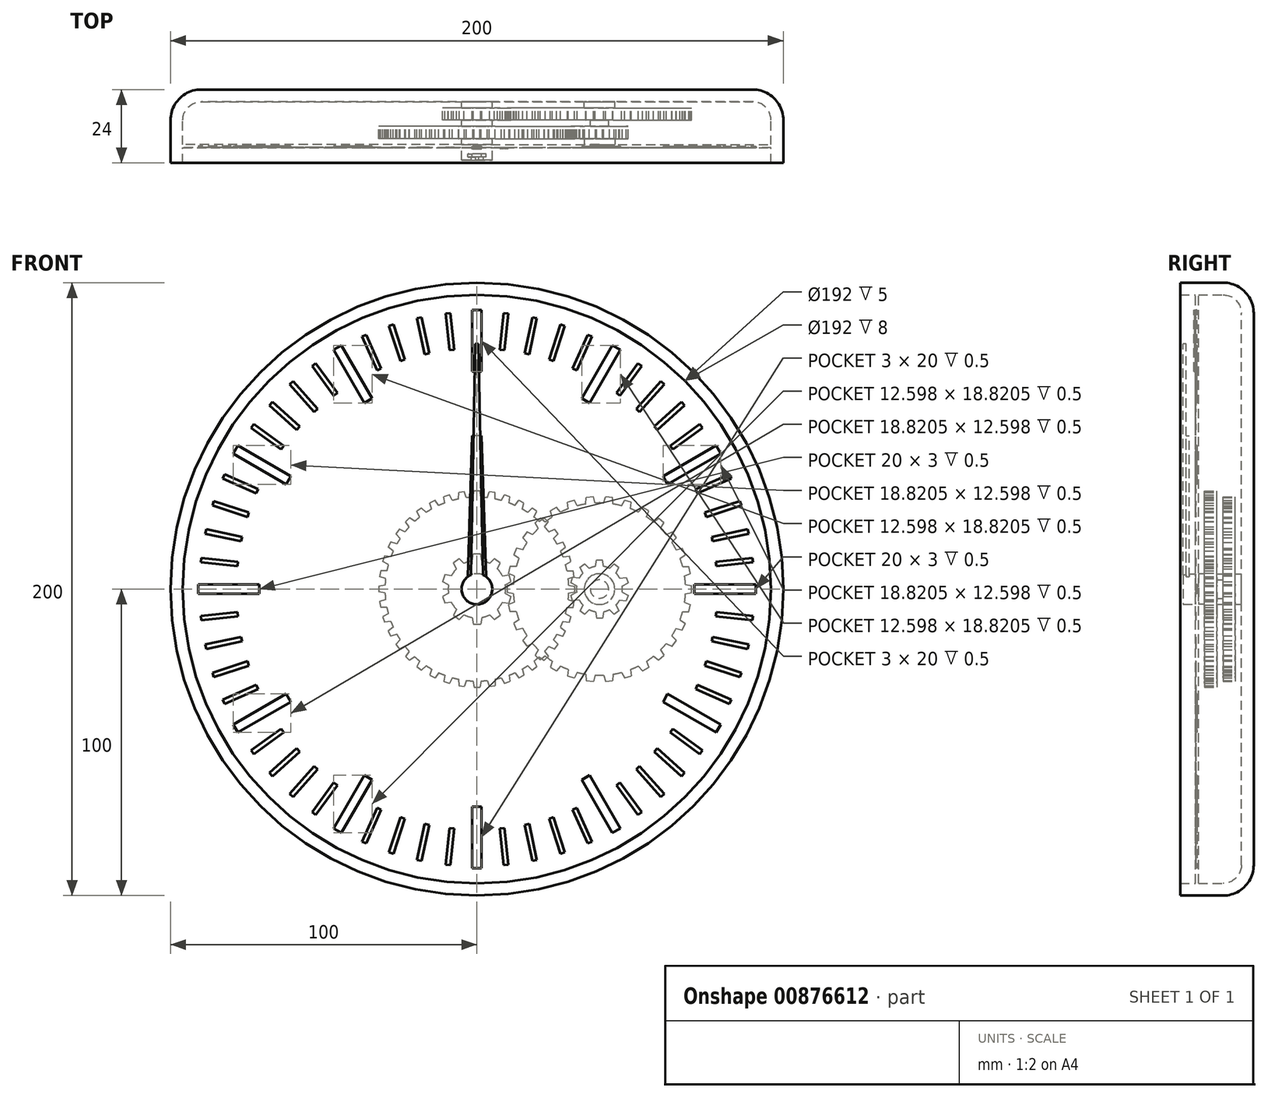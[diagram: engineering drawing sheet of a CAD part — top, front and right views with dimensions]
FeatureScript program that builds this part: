
annotation { "Feature Type Name" : "Feature", "Feature Type Description" : "" }
export const myFeature = defineFeature(function(context is Context, id is Id, definition is map)
    precondition{}
    {
        {
            var Q0;
            Q0=qCreatedBy(makeId("Front.planeOp"),FACE);
            var sketch = newSketch(context, id + "F0", { "sketchPlane" : qUnion([Q0])});
            skCircle(sketch, "E0", {"center": v(0, 0) * mm, "radius": 100 * mm});
            skSolve(sketch);
        }
        {
            var Q0;
            Q0 = qSketchRegion(id + "F0", true);
            extrude(context, id + "F1", {"entities" : qUnion([Q0]), "depth" : 24 * mm, "offsetDistance" : 25 * mm});
        }
        {
            var Q0;
            Q0=makeQuery(id+"F1.opExtrude","CAP_EDGE",EDGE,{"disambiguationData":[OSD([sQuery(id+"F0.wireOp",EDGE,"E0")])],"isStart":true});
            fillet(context, id + "F2", {"entities" : qUnion([Q0]), "radius" : 10 * mm, "tangentPropagation" : true, "allowEdgeOverflow" : false});
        }
        {
            var Q0;
            Q0=makeQuery(id+"F1.opExtrude","CAP_FACE",FACE,{"disambiguationData":[OSD([sQuery(id+"F0.wireOp",EDGE,"E0")])],"isStart":false});
            shell(context, id + "F3", {"entities" : qUnion([Q0]), "thickness" : 4 * mm});
        }
        {
            var Q0;
            {var subQ0=sQuery(id+"F0.wireOp",EDGE,"E0");Q0=makeQuery(id+"F3.opShell","OFFSET_FACE",FACE,{"disambiguationData":[OSD([subQ0]),TDD([makeQuery(id+"F1.opExtrude","CAP_FACE",FACE,{"disambiguationData":[OSD([subQ0])],"isStart":true})])]});}
            var sketch = newSketch(context, id + "F4", { "sketchPlane" : qUnion([Q0])});
            skCircle(sketch, "E1", {"center": v(0, 0) * mm, "radius": 3 * mm});
            skCircle(sketch, "E2", {"center": v(0, 0) * mm, "radius": 5 * mm});
            skCircle(sketch, "E3", {"center": v(40, 0) * mm, "radius": 3 * mm});
            skCircle(sketch, "E4", {"center": v(40, 0) * mm, "radius": 5 * mm});
            skSolve(sketch);
        }
        {
            var Q0;
            Q0 = qSketchRegion(id + "F4", true);
            extrude(context, id + "F5", {"entities" : qUnion([Q0]), "operationType" : NewBodyOperationType.ADD, "depth" : 2 * mm, "offsetDistance" : 25 * mm});
        }
        {
            var Q0;
            {var subQ0=sQuery(id+"F0.wireOp",EDGE,"E0");Q0=makeQuery(id+"F5.boolean.opBoolean","SPLIT",FACE,{"disambiguationData":[TD([makeQuery(id+"F5.opExtrude","SWEPT_FACE",FACE,{"disambiguationData":[OSD([sQuery(id+"F4.wireOp",EDGE,"E1")])]})])],"derivedFrom":makeQuery(id+"F3.opShell","OFFSET_FACE",FACE,{"disambiguationData":[OSD([subQ0]),TDD([makeQuery(id+"F1.opExtrude","CAP_FACE",FACE,{"disambiguationData":[OSD([subQ0])],"isStart":true})])]})});}
            extrude(context, id + "F6", {"entities" : qUnion([Q0]), "depth" : 19 * mm, "offsetDistance" : 25 * mm});
        }
        {
            var Q0;
            {var subQ0=sQuery(id+"F0.wireOp",EDGE,"E0");Q0=makeQuery(id+"F5.boolean.opBoolean","SPLIT",FACE,{"disambiguationData":[TD([makeQuery(id+"F5.opExtrude","SWEPT_FACE",FACE,{"disambiguationData":[OSD([sQuery(id+"F4.wireOp",EDGE,"E3")])]})])],"derivedFrom":makeQuery(id+"F3.opShell","OFFSET_FACE",FACE,{"disambiguationData":[OSD([subQ0]),TDD([makeQuery(id+"F1.opExtrude","CAP_FACE",FACE,{"disambiguationData":[OSD([subQ0])],"isStart":true})])]})});}
            extrude(context, id + "F7", {"entities" : qUnion([Q0]), "depth" : 8 * mm, "offsetDistance" : 25 * mm});
        }
        {
            var Q0;
            Q0=makeQuery(id+"F5.opExtrude","CAP_FACE",FACE,{"disambiguationData":[OSD([sQuery(id+"F4.wireOp",EDGE,"E1"),sQuery(id+"F4.wireOp",EDGE,"E2")])],"isStart":false});
            var sketch = newSketch(context, id + "F8", { "sketchPlane" : qUnion([Q0])});
            skCircle(sketch, "E5", {"center": v(0, 0) * mm, "radius": 9.38 * mm});
            skLineSegment(sketch, "E6", {"start": v(1.55, 9.25) * mm, "end": v(1.18, 11.38) * mm});
            skLineSegment(sketch, "E7", {"start": v(1.18, 11.38) * mm, "end": v(0, 11.38) * mm});
            skLineSegment(sketch, "E8.MirrorCS", {"start": v(-1.18, 11.38) * mm, "end": v(0, 11.38) * mm});
            skLineSegment(sketch, "E9.MirrorCS", {"start": v(-1.55, 9.25) * mm, "end": v(-1.18, 11.38) * mm});
            skLineSegment(sketch, "E10.1.0", {"start": v(-4.18, 8.4) * mm, "end": v(-5.73, 9.9) * mm});
            skLineSegment(sketch, "E10.1.1", {"start": v(-5.73, 9.9) * mm, "end": v(-6.69, 9.2) * mm});
            skLineSegment(sketch, "E10.1.2", {"start": v(-7.64, 8.51) * mm, "end": v(-6.69, 9.2) * mm});
            skLineSegment(sketch, "E10.1.3", {"start": v(-6.7, 6.57) * mm, "end": v(-7.64, 8.51) * mm});
            skLineSegment(sketch, "E10.2.0", {"start": v(-8.31, 4.33) * mm, "end": v(-10.45, 4.64) * mm});
            skLineSegment(sketch, "E10.2.1", {"start": v(-10.45, 4.64) * mm, "end": v(-10.82, 3.52) * mm});
            skLineSegment(sketch, "E10.2.2", {"start": v(-11.18, 2.4) * mm, "end": v(-10.82, 3.52) * mm});
            skLineSegment(sketch, "E10.2.3", {"start": v(-9.27, 1.38) * mm, "end": v(-11.18, 2.4) * mm});
            skLineSegment(sketch, "E11.1.3.0", {"start": v(-9.27, -1.38) * mm, "end": v(-11.18, -2.4) * mm});
            skLineSegment(sketch, "E11.3.3.0", {"start": v(-11.18, -2.4) * mm, "end": v(-10.82, -3.52) * mm});
            skLineSegment(sketch, "E11.6.3.0", {"start": v(-10.45, -4.64) * mm, "end": v(-10.82, -3.52) * mm});
            skLineSegment(sketch, "E11.9.3.0", {"start": v(-8.31, -4.33) * mm, "end": v(-10.45, -4.64) * mm});
            skLineSegment(sketch, "E11.1.4.0", {"start": v(-6.7, -6.57) * mm, "end": v(-7.64, -8.51) * mm});
            skLineSegment(sketch, "E11.3.4.0", {"start": v(-7.64, -8.51) * mm, "end": v(-6.69, -9.2) * mm});
            skLineSegment(sketch, "E11.6.4.0", {"start": v(-5.73, -9.9) * mm, "end": v(-6.69, -9.2) * mm});
            skLineSegment(sketch, "E11.9.4.0", {"start": v(-4.18, -8.4) * mm, "end": v(-5.73, -9.9) * mm});
            skLineSegment(sketch, "E11.1.5.0", {"start": v(-1.55, -9.25) * mm, "end": v(-1.18, -11.38) * mm});
            skLineSegment(sketch, "E11.3.5.0", {"start": v(-1.18, -11.38) * mm, "end": v(0, -11.38) * mm});
            skLineSegment(sketch, "E11.6.5.0", {"start": v(1.18, -11.38) * mm, "end": v(0, -11.38) * mm});
            skLineSegment(sketch, "E11.9.5.0", {"start": v(1.55, -9.25) * mm, "end": v(1.18, -11.38) * mm});
            skLineSegment(sketch, "E11.1.6.0", {"start": v(4.18, -8.4) * mm, "end": v(5.73, -9.9) * mm});
            skLineSegment(sketch, "E11.3.6.0", {"start": v(5.73, -9.9) * mm, "end": v(6.69, -9.2) * mm});
            skLineSegment(sketch, "E11.6.6.0", {"start": v(7.64, -8.51) * mm, "end": v(6.69, -9.2) * mm});
            skLineSegment(sketch, "E11.9.6.0", {"start": v(6.7, -6.57) * mm, "end": v(7.64, -8.51) * mm});
            skLineSegment(sketch, "E11.1.7.0", {"start": v(8.31, -4.33) * mm, "end": v(10.45, -4.64) * mm});
            skLineSegment(sketch, "E11.3.7.0", {"start": v(10.45, -4.64) * mm, "end": v(10.82, -3.52) * mm});
            skLineSegment(sketch, "E11.6.7.0", {"start": v(11.18, -2.4) * mm, "end": v(10.82, -3.52) * mm});
            skLineSegment(sketch, "E11.9.7.0", {"start": v(9.27, -1.38) * mm, "end": v(11.18, -2.4) * mm});
            skLineSegment(sketch, "E11.1.8.0", {"start": v(9.27, 1.38) * mm, "end": v(11.18, 2.4) * mm});
            skLineSegment(sketch, "E11.3.8.0", {"start": v(11.18, 2.4) * mm, "end": v(10.82, 3.52) * mm});
            skLineSegment(sketch, "E11.6.8.0", {"start": v(10.45, 4.64) * mm, "end": v(10.82, 3.52) * mm});
            skLineSegment(sketch, "E11.9.8.0", {"start": v(8.31, 4.33) * mm, "end": v(10.45, 4.64) * mm});
            skLineSegment(sketch, "E11.1.9.0", {"start": v(6.7, 6.57) * mm, "end": v(7.64, 8.51) * mm});
            skLineSegment(sketch, "E11.3.9.0", {"start": v(7.64, 8.51) * mm, "end": v(6.69, 9.2) * mm});
            skLineSegment(sketch, "E11.6.9.0", {"start": v(5.73, 9.9) * mm, "end": v(6.69, 9.2) * mm});
            skLineSegment(sketch, "E11.9.9.0", {"start": v(4.18, 8.4) * mm, "end": v(5.73, 9.9) * mm});
            skSolve(sketch);
        }
        {
            var Q0;
            Q0 = qSketchRegion(id + "F8", true);
            extrude(context, id + "F9", {"entities" : qUnion([Q0]), "operationType" : NewBodyOperationType.ADD, "depth" : 4 * mm, "offsetDistance" : 25 * mm});
        }
        {
            var Q0;
            Q0=makeQuery(id+"F5.opExtrude","CAP_FACE",FACE,{"disambiguationData":[OSD([sQuery(id+"F4.wireOp",EDGE,"E3"),sQuery(id+"F4.wireOp",EDGE,"E4")])],"isStart":false});
            var sketch = newSketch(context, id + "F10", { "sketchPlane" : qUnion([Q0])});
            skCircle(sketch, "E12", {"center": v(40, 0) * mm, "radius": 28.13 * mm});
            skLineSegment(sketch, "E13", {"start": v(11.92, 1.54) * mm, "end": v(9.88, 1.18) * mm});
            skLineSegment(sketch, "E14", {"start": v(9.88, 1.18) * mm, "end": v(9.88, 0) * mm});
            skLineSegment(sketch, "E15.MirrorCS", {"start": v(9.88, -1.18) * mm, "end": v(9.88, 0) * mm});
            skLineSegment(sketch, "E16.MirrorCS", {"start": v(11.92, -1.54) * mm, "end": v(9.88, -1.18) * mm});
            skLineSegment(sketch, "E17.1.0", {"start": v(12.21, -4.33) * mm, "end": v(10.29, -5.11) * mm});
            skLineSegment(sketch, "E17.1.1", {"start": v(10.29, -5.11) * mm, "end": v(10.53, -6.26) * mm});
            skLineSegment(sketch, "E17.1.2", {"start": v(10.78, -7.42) * mm, "end": v(10.53, -6.26) * mm});
            skLineSegment(sketch, "E17.1.3", {"start": v(12.85, -7.34) * mm, "end": v(10.78, -7.42) * mm});
            skLineSegment(sketch, "E17.2.0", {"start": v(13.72, -10.02) * mm, "end": v(12, -11.18) * mm});
            skLineSegment(sketch, "E17.2.1", {"start": v(12, -11.18) * mm, "end": v(12.48, -12.25) * mm});
            skLineSegment(sketch, "E17.2.2", {"start": v(12.96, -13.33) * mm, "end": v(12.48, -12.25) * mm});
            skLineSegment(sketch, "E17.2.3", {"start": v(14.97, -12.83) * mm, "end": v(12.96, -13.33) * mm});
            skLineSegment(sketch, "E18.2.3.0", {"start": v(16.38, -15.26) * mm, "end": v(14.94, -16.75) * mm});
            skLineSegment(sketch, "E18.3.3.0", {"start": v(14.94, -16.75) * mm, "end": v(15.63, -17.7) * mm});
            skLineSegment(sketch, "E18.6.3.0", {"start": v(16.32, -18.66) * mm, "end": v(15.63, -17.7) * mm});
            skLineSegment(sketch, "E18.9.3.0", {"start": v(18.18, -17.75) * mm, "end": v(16.32, -18.66) * mm});
            skLineSegment(sketch, "E18.2.4.0", {"start": v(20.07, -19.84) * mm, "end": v(18.97, -21.6) * mm});
            skLineSegment(sketch, "E18.3.4.0", {"start": v(18.97, -21.6) * mm, "end": v(19.84, -22.39) * mm});
            skLineSegment(sketch, "E18.6.4.0", {"start": v(20.72, -23.18) * mm, "end": v(19.84, -22.39) * mm});
            skLineSegment(sketch, "E18.9.4.0", {"start": v(22.35, -21.9) * mm, "end": v(20.72, -23.18) * mm});
            skLineSegment(sketch, "E18.2.5.0", {"start": v(24.63, -23.55) * mm, "end": v(23.92, -25.5) * mm});
            skLineSegment(sketch, "E18.3.5.0", {"start": v(23.92, -25.5) * mm, "end": v(24.94, -26.09) * mm});
            skLineSegment(sketch, "E18.6.5.0", {"start": v(25.96, -26.68) * mm, "end": v(24.94, -26.09) * mm});
            skLineSegment(sketch, "E18.9.5.0", {"start": v(27.3, -25.09) * mm, "end": v(25.96, -26.68) * mm});
            skLineSegment(sketch, "E18.2.6.0", {"start": v(29.86, -26.23) * mm, "end": v(29.57, -28.29) * mm});
            skLineSegment(sketch, "E18.3.6.0", {"start": v(29.57, -28.29) * mm, "end": v(30.7, -28.65) * mm});
            skLineSegment(sketch, "E18.6.6.0", {"start": v(31.81, -29.01) * mm, "end": v(30.7, -28.65) * mm});
            skLineSegment(sketch, "E18.9.6.0", {"start": v(32.78, -27.18) * mm, "end": v(31.81, -29.01) * mm});
            skLineSegment(sketch, "E18.2.7.0", {"start": v(35.53, -27.77) * mm, "end": v(35.68, -29.84) * mm});
            skLineSegment(sketch, "E18.3.7.0", {"start": v(35.68, -29.84) * mm, "end": v(36.85, -29.96) * mm});
            skLineSegment(sketch, "E18.6.7.0", {"start": v(38.02, -30.08) * mm, "end": v(36.85, -29.96) * mm});
            skLineSegment(sketch, "E18.9.7.0", {"start": v(38.6, -28.09) * mm, "end": v(38.02, -30.08) * mm});
            skLineSegment(sketch, "E18.2.8.0", {"start": v(41.4, -28.09) * mm, "end": v(41.98, -30.08) * mm});
            skLineSegment(sketch, "E18.3.8.0", {"start": v(41.98, -30.08) * mm, "end": v(43.15, -29.96) * mm});
            skLineSegment(sketch, "E18.6.8.0", {"start": v(44.32, -29.84) * mm, "end": v(43.15, -29.96) * mm});
            skLineSegment(sketch, "E18.9.8.0", {"start": v(44.47, -27.77) * mm, "end": v(44.32, -29.84) * mm});
            skLineSegment(sketch, "E18.2.9.0", {"start": v(47.22, -27.18) * mm, "end": v(48.19, -29.01) * mm});
            skLineSegment(sketch, "E18.3.9.0", {"start": v(48.19, -29.01) * mm, "end": v(49.3, -28.65) * mm});
            skLineSegment(sketch, "E18.6.9.0", {"start": v(50.43, -28.29) * mm, "end": v(49.3, -28.65) * mm});
            skLineSegment(sketch, "E18.9.9.0", {"start": v(50.14, -26.23) * mm, "end": v(50.43, -28.29) * mm});
            skLineSegment(sketch, "E18.2.10.0", {"start": v(52.7, -25.09) * mm, "end": v(54.04, -26.68) * mm});
            skLineSegment(sketch, "E18.3.10.0", {"start": v(54.04, -26.68) * mm, "end": v(55.06, -26.09) * mm});
            skLineSegment(sketch, "E18.6.10.0", {"start": v(56.08, -25.5) * mm, "end": v(55.06, -26.09) * mm});
            skLineSegment(sketch, "E18.9.10.0", {"start": v(55.37, -23.55) * mm, "end": v(56.08, -25.5) * mm});
            skLineSegment(sketch, "E18.2.11.0", {"start": v(57.65, -21.9) * mm, "end": v(59.28, -23.18) * mm});
            skLineSegment(sketch, "E18.3.11.0", {"start": v(59.28, -23.18) * mm, "end": v(60.16, -22.39) * mm});
            skLineSegment(sketch, "E18.6.11.0", {"start": v(61.03, -21.6) * mm, "end": v(60.16, -22.39) * mm});
            skLineSegment(sketch, "E18.9.11.0", {"start": v(59.93, -19.84) * mm, "end": v(61.03, -21.6) * mm});
            skLineSegment(sketch, "E18.2.12.0", {"start": v(61.82, -17.75) * mm, "end": v(63.68, -18.66) * mm});
            skLineSegment(sketch, "E18.3.12.0", {"start": v(63.68, -18.66) * mm, "end": v(64.37, -17.7) * mm});
            skLineSegment(sketch, "E18.6.12.0", {"start": v(65.06, -16.75) * mm, "end": v(64.37, -17.7) * mm});
            skLineSegment(sketch, "E18.9.12.0", {"start": v(63.62, -15.26) * mm, "end": v(65.06, -16.75) * mm});
            skLineSegment(sketch, "E18.2.13.0", {"start": v(65.03, -12.83) * mm, "end": v(67.04, -13.33) * mm});
            skLineSegment(sketch, "E18.3.13.0", {"start": v(67.04, -13.33) * mm, "end": v(67.52, -12.25) * mm});
            skLineSegment(sketch, "E18.6.13.0", {"start": v(68, -11.18) * mm, "end": v(67.52, -12.25) * mm});
            skLineSegment(sketch, "E18.9.13.0", {"start": v(66.28, -10.02) * mm, "end": v(68, -11.18) * mm});
            skLineSegment(sketch, "E18.2.14.0", {"start": v(67.15, -7.34) * mm, "end": v(69.22, -7.42) * mm});
            skLineSegment(sketch, "E18.3.14.0", {"start": v(69.22, -7.42) * mm, "end": v(69.47, -6.26) * mm});
            skLineSegment(sketch, "E18.6.14.0", {"start": v(69.71, -5.11) * mm, "end": v(69.47, -6.26) * mm});
            skLineSegment(sketch, "E18.9.14.0", {"start": v(67.79, -4.33) * mm, "end": v(69.71, -5.11) * mm});
            skLineSegment(sketch, "E18.2.15.0", {"start": v(68.08, -1.54) * mm, "end": v(70.12, -1.18) * mm});
            skLineSegment(sketch, "E18.3.15.0", {"start": v(70.12, -1.18) * mm, "end": v(70.12, 0) * mm});
            skLineSegment(sketch, "E18.6.15.0", {"start": v(70.12, 1.18) * mm, "end": v(70.12, 0) * mm});
            skLineSegment(sketch, "E18.9.15.0", {"start": v(68.08, 1.54) * mm, "end": v(70.12, 1.18) * mm});
            skLineSegment(sketch, "E18.2.16.0", {"start": v(67.79, 4.33) * mm, "end": v(69.71, 5.11) * mm});
            skLineSegment(sketch, "E18.3.16.0", {"start": v(69.71, 5.11) * mm, "end": v(69.47, 6.26) * mm});
            skLineSegment(sketch, "E18.6.16.0", {"start": v(69.22, 7.42) * mm, "end": v(69.47, 6.26) * mm});
            skLineSegment(sketch, "E18.9.16.0", {"start": v(67.15, 7.34) * mm, "end": v(69.22, 7.42) * mm});
            skLineSegment(sketch, "E18.2.17.0", {"start": v(66.28, 10.02) * mm, "end": v(68, 11.18) * mm});
            skLineSegment(sketch, "E18.3.17.0", {"start": v(68, 11.18) * mm, "end": v(67.52, 12.25) * mm});
            skLineSegment(sketch, "E18.6.17.0", {"start": v(67.04, 13.33) * mm, "end": v(67.52, 12.25) * mm});
            skLineSegment(sketch, "E18.9.17.0", {"start": v(65.03, 12.83) * mm, "end": v(67.04, 13.33) * mm});
            skLineSegment(sketch, "E18.2.18.0", {"start": v(63.62, 15.26) * mm, "end": v(65.06, 16.75) * mm});
            skLineSegment(sketch, "E18.3.18.0", {"start": v(65.06, 16.75) * mm, "end": v(64.37, 17.7) * mm});
            skLineSegment(sketch, "E18.6.18.0", {"start": v(63.68, 18.66) * mm, "end": v(64.37, 17.7) * mm});
            skLineSegment(sketch, "E18.9.18.0", {"start": v(61.82, 17.75) * mm, "end": v(63.68, 18.66) * mm});
            skLineSegment(sketch, "E18.2.19.0", {"start": v(59.93, 19.84) * mm, "end": v(61.03, 21.6) * mm});
            skLineSegment(sketch, "E18.3.19.0", {"start": v(61.03, 21.6) * mm, "end": v(60.16, 22.39) * mm});
            skLineSegment(sketch, "E18.6.19.0", {"start": v(59.28, 23.18) * mm, "end": v(60.16, 22.39) * mm});
            skLineSegment(sketch, "E18.9.19.0", {"start": v(57.65, 21.9) * mm, "end": v(59.28, 23.18) * mm});
            skLineSegment(sketch, "E18.2.20.0", {"start": v(55.37, 23.55) * mm, "end": v(56.08, 25.5) * mm});
            skLineSegment(sketch, "E18.3.20.0", {"start": v(56.08, 25.5) * mm, "end": v(55.06, 26.09) * mm});
            skLineSegment(sketch, "E18.6.20.0", {"start": v(54.04, 26.68) * mm, "end": v(55.06, 26.09) * mm});
            skLineSegment(sketch, "E18.9.20.0", {"start": v(52.7, 25.09) * mm, "end": v(54.04, 26.68) * mm});
            skLineSegment(sketch, "E18.2.21.0", {"start": v(50.14, 26.23) * mm, "end": v(50.43, 28.29) * mm});
            skLineSegment(sketch, "E18.3.21.0", {"start": v(50.43, 28.29) * mm, "end": v(49.3, 28.65) * mm});
            skLineSegment(sketch, "E18.6.21.0", {"start": v(48.19, 29.01) * mm, "end": v(49.3, 28.65) * mm});
            skLineSegment(sketch, "E18.9.21.0", {"start": v(47.22, 27.18) * mm, "end": v(48.19, 29.01) * mm});
            skLineSegment(sketch, "E18.2.22.0", {"start": v(44.47, 27.77) * mm, "end": v(44.32, 29.84) * mm});
            skLineSegment(sketch, "E18.3.22.0", {"start": v(44.32, 29.84) * mm, "end": v(43.15, 29.96) * mm});
            skLineSegment(sketch, "E18.6.22.0", {"start": v(41.98, 30.08) * mm, "end": v(43.15, 29.96) * mm});
            skLineSegment(sketch, "E18.9.22.0", {"start": v(41.4, 28.09) * mm, "end": v(41.98, 30.08) * mm});
            skLineSegment(sketch, "E18.2.23.0", {"start": v(38.6, 28.09) * mm, "end": v(38.02, 30.08) * mm});
            skLineSegment(sketch, "E18.3.23.0", {"start": v(38.02, 30.08) * mm, "end": v(36.85, 29.96) * mm});
            skLineSegment(sketch, "E18.6.23.0", {"start": v(35.68, 29.84) * mm, "end": v(36.85, 29.96) * mm});
            skLineSegment(sketch, "E18.9.23.0", {"start": v(35.53, 27.77) * mm, "end": v(35.68, 29.84) * mm});
            skLineSegment(sketch, "E18.2.24.0", {"start": v(32.78, 27.18) * mm, "end": v(31.81, 29.01) * mm});
            skLineSegment(sketch, "E18.3.24.0", {"start": v(31.81, 29.01) * mm, "end": v(30.7, 28.65) * mm});
            skLineSegment(sketch, "E18.6.24.0", {"start": v(29.57, 28.29) * mm, "end": v(30.7, 28.65) * mm});
            skLineSegment(sketch, "E18.9.24.0", {"start": v(29.86, 26.23) * mm, "end": v(29.57, 28.29) * mm});
            skLineSegment(sketch, "E18.2.25.0", {"start": v(27.3, 25.09) * mm, "end": v(25.96, 26.68) * mm});
            skLineSegment(sketch, "E18.3.25.0", {"start": v(25.96, 26.68) * mm, "end": v(24.94, 26.09) * mm});
            skLineSegment(sketch, "E18.6.25.0", {"start": v(23.92, 25.5) * mm, "end": v(24.94, 26.09) * mm});
            skLineSegment(sketch, "E18.9.25.0", {"start": v(24.63, 23.55) * mm, "end": v(23.92, 25.5) * mm});
            skLineSegment(sketch, "E18.2.26.0", {"start": v(22.35, 21.9) * mm, "end": v(20.72, 23.18) * mm});
            skLineSegment(sketch, "E18.3.26.0", {"start": v(20.72, 23.18) * mm, "end": v(19.84, 22.39) * mm});
            skLineSegment(sketch, "E18.6.26.0", {"start": v(18.97, 21.6) * mm, "end": v(19.84, 22.39) * mm});
            skLineSegment(sketch, "E18.9.26.0", {"start": v(20.07, 19.84) * mm, "end": v(18.97, 21.6) * mm});
            skLineSegment(sketch, "E18.2.27.0", {"start": v(18.18, 17.75) * mm, "end": v(16.32, 18.66) * mm});
            skLineSegment(sketch, "E18.3.27.0", {"start": v(16.32, 18.66) * mm, "end": v(15.63, 17.7) * mm});
            skLineSegment(sketch, "E18.6.27.0", {"start": v(14.94, 16.75) * mm, "end": v(15.63, 17.7) * mm});
            skLineSegment(sketch, "E18.9.27.0", {"start": v(16.38, 15.26) * mm, "end": v(14.94, 16.75) * mm});
            skLineSegment(sketch, "E18.2.28.0", {"start": v(14.97, 12.83) * mm, "end": v(12.96, 13.33) * mm});
            skLineSegment(sketch, "E18.3.28.0", {"start": v(12.96, 13.33) * mm, "end": v(12.48, 12.25) * mm});
            skLineSegment(sketch, "E18.6.28.0", {"start": v(12, 11.18) * mm, "end": v(12.48, 12.25) * mm});
            skLineSegment(sketch, "E18.9.28.0", {"start": v(13.72, 10.02) * mm, "end": v(12, 11.18) * mm});
            skLineSegment(sketch, "E18.2.29.0", {"start": v(12.85, 7.34) * mm, "end": v(10.78, 7.42) * mm});
            skLineSegment(sketch, "E18.3.29.0", {"start": v(10.78, 7.42) * mm, "end": v(10.53, 6.26) * mm});
            skLineSegment(sketch, "E18.6.29.0", {"start": v(10.29, 5.11) * mm, "end": v(10.53, 6.26) * mm});
            skLineSegment(sketch, "E18.9.29.0", {"start": v(12.21, 4.33) * mm, "end": v(10.29, 5.11) * mm});
            skSolve(sketch);
        }
        {
            var Q0;
            Q0 = qSketchRegion(id + "F10", true);
            extrude(context, id + "F11", {"entities" : qUnion([Q0]), "operationType" : NewBodyOperationType.ADD, "depth" : 4 * mm, "offsetDistance" : 25 * mm});
        }
        {
            var Q0;
            Q0=makeQuery(id+"F9.opExtrude","CAP_FACE",FACE,{"disambiguationData":[OSD([sQuery(id+"F8.wireOp",EDGE,"E5"),sQuery(id+"F8.wireOp",EDGE,"E6"),sQuery(id+"F8.wireOp",EDGE,"E7"),sQuery(id+"F8.wireOp",EDGE,"E8.MirrorCS"),sQuery(id+"F8.wireOp",EDGE,"E9.MirrorCS"),sQuery(id+"F8.wireOp",EDGE,"E10.1.0"),sQuery(id+"F8.wireOp",EDGE,"E10.1.1"),sQuery(id+"F8.wireOp",EDGE,"E10.1.2"),sQuery(id+"F8.wireOp",EDGE,"E10.1.3"),sQuery(id+"F8.wireOp",EDGE,"E10.2.0"),sQuery(id+"F8.wireOp",EDGE,"E10.2.1"),sQuery(id+"F8.wireOp",EDGE,"E10.2.2"),sQuery(id+"F8.wireOp",EDGE,"E10.2.3"),sQuery(id+"F8.wireOp",EDGE,"E11.1.3.0"),sQuery(id+"F8.wireOp",EDGE,"E11.3.3.0"),sQuery(id+"F8.wireOp",EDGE,"E11.6.3.0"),sQuery(id+"F8.wireOp",EDGE,"E11.9.3.0"),sQuery(id+"F8.wireOp",EDGE,"E11.1.4.0"),sQuery(id+"F8.wireOp",EDGE,"E11.3.4.0"),sQuery(id+"F8.wireOp",EDGE,"E11.6.4.0"),sQuery(id+"F8.wireOp",EDGE,"E11.9.4.0"),sQuery(id+"F8.wireOp",EDGE,"E11.1.5.0"),sQuery(id+"F8.wireOp",EDGE,"E11.3.5.0"),sQuery(id+"F8.wireOp",EDGE,"E11.6.5.0"),sQuery(id+"F8.wireOp",EDGE,"E11.9.5.0"),sQuery(id+"F8.wireOp",EDGE,"E11.1.6.0"),sQuery(id+"F8.wireOp",EDGE,"E11.3.6.0"),sQuery(id+"F8.wireOp",EDGE,"E11.6.6.0"),sQuery(id+"F8.wireOp",EDGE,"E11.9.6.0"),sQuery(id+"F8.wireOp",EDGE,"E11.1.7.0"),sQuery(id+"F8.wireOp",EDGE,"E11.3.7.0"),sQuery(id+"F8.wireOp",EDGE,"E11.6.7.0"),sQuery(id+"F8.wireOp",EDGE,"E11.9.7.0"),sQuery(id+"F8.wireOp",EDGE,"E11.1.8.0"),sQuery(id+"F8.wireOp",EDGE,"E11.3.8.0"),sQuery(id+"F8.wireOp",EDGE,"E11.6.8.0"),sQuery(id+"F8.wireOp",EDGE,"E11.9.8.0"),sQuery(id+"F8.wireOp",EDGE,"E11.1.9.0"),sQuery(id+"F8.wireOp",EDGE,"E11.3.9.0"),sQuery(id+"F8.wireOp",EDGE,"E11.6.9.0"),sQuery(id+"F8.wireOp",EDGE,"E11.9.9.0")])],"isStart":false});
            var sketch = newSketch(context, id + "F12", { "sketchPlane" : qUnion([Q0])});
            skCircle(sketch, "E19.0", {"center": v(0, 0) * mm, "radius": 3 * mm});
            skCircle(sketch, "E20.0", {"center": v(0, 0) * mm, "radius": 5 * mm});
            skSolve(sketch);
        }
        {
            var Q0;
            Q0 = qSketchRegion(id + "F12", true);
            extrude(context, id + "F13", {"entities" : qUnion([Q0]), "depth" : 2 * mm, "offsetDistance" : 25 * mm});
        }
        {
            var Q0;
            Q0=makeQuery(id+"F13.opExtrude","CAP_FACE",FACE,{"disambiguationData":[OSD([sQuery(id+"F12.wireOp",EDGE,"E19.0"),sQuery(id+"F12.wireOp",EDGE,"E20.0")])],"isStart":false});
            var sketch = newSketch(context, id + "F14", { "sketchPlane" : qUnion([Q0])});
            skCircle(sketch, "E21.0", {"center": v(0, 0) * mm, "radius": 3 * mm});
            skCircle(sketch, "E22", {"center": v(0, 0) * mm, "radius": 30 * mm});
            skLineSegment(sketch, "E23", {"start": v(1.3, 29.97) * mm, "end": v(0.94, 32) * mm});
            skLineSegment(sketch, "E24", {"start": v(0.94, 32) * mm, "end": v(0, 32) * mm});
            skLineSegment(sketch, "E25.MirrorCS", {"start": v(-0.94, 32) * mm, "end": v(0, 32) * mm});
            skLineSegment(sketch, "E26.MirrorCS", {"start": v(-1.3, 29.97) * mm, "end": v(-0.94, 32) * mm});
            skLineSegment(sketch, "E27.1.0", {"start": v(-5.97, 29.4) * mm, "end": v(-5.94, 31.46) * mm});
            skLineSegment(sketch, "E27.1.1", {"start": v(-5.94, 31.46) * mm, "end": v(-5, 31.6) * mm});
            skLineSegment(sketch, "E27.1.2", {"start": v(-4.08, 31.75) * mm, "end": v(-5, 31.6) * mm});
            skLineSegment(sketch, "E27.1.3", {"start": v(-3.4, 29.8) * mm, "end": v(-4.08, 31.75) * mm});
            skLineSegment(sketch, "E27.2.0", {"start": v(-10.5, 28.1) * mm, "end": v(-10.78, 30.14) * mm});
            skLineSegment(sketch, "E27.2.1", {"start": v(-10.78, 30.14) * mm, "end": v(-9.89, 30.43) * mm});
            skLineSegment(sketch, "E27.2.2", {"start": v(-9, 30.73) * mm, "end": v(-9.89, 30.43) * mm});
            skLineSegment(sketch, "E27.2.3", {"start": v(-8.03, 28.9) * mm, "end": v(-9, 30.73) * mm});
            skLineSegment(sketch, "E28.1.3.0", {"start": v(-14.77, 26.11) * mm, "end": v(-15.37, 28.08) * mm});
            skLineSegment(sketch, "E28.3.3.0", {"start": v(-15.37, 28.08) * mm, "end": v(-14.53, 28.51) * mm});
            skLineSegment(sketch, "E28.6.3.0", {"start": v(-13.69, 28.94) * mm, "end": v(-14.53, 28.51) * mm});
            skLineSegment(sketch, "E28.9.3.0", {"start": v(-12.45, 27.3) * mm, "end": v(-13.69, 28.94) * mm});
            skLineSegment(sketch, "E28.1.4.0", {"start": v(-18.67, 23.48) * mm, "end": v(-19.57, 25.33) * mm});
            skLineSegment(sketch, "E28.3.4.0", {"start": v(-19.57, 25.33) * mm, "end": v(-18.8, 25.89) * mm});
            skLineSegment(sketch, "E28.6.4.0", {"start": v(-18.05, 26.44) * mm, "end": v(-18.8, 25.89) * mm});
            skLineSegment(sketch, "E28.9.4.0", {"start": v(-16.57, 25.01) * mm, "end": v(-18.05, 26.44) * mm});
            skLineSegment(sketch, "E28.1.5.0", {"start": v(-22.11, 20.27) * mm, "end": v(-23.3, 21.96) * mm});
            skLineSegment(sketch, "E28.3.5.0", {"start": v(-23.3, 21.96) * mm, "end": v(-22.63, 22.63) * mm});
            skLineSegment(sketch, "E28.6.5.0", {"start": v(-21.96, 23.3) * mm, "end": v(-22.63, 22.63) * mm});
            skLineSegment(sketch, "E28.9.5.0", {"start": v(-20.27, 22.11) * mm, "end": v(-21.96, 23.3) * mm});
            skLineSegment(sketch, "E28.1.6.0", {"start": v(-25.01, 16.57) * mm, "end": v(-26.44, 18.05) * mm});
            skLineSegment(sketch, "E28.3.6.0", {"start": v(-26.44, 18.05) * mm, "end": v(-25.89, 18.8) * mm});
            skLineSegment(sketch, "E28.6.6.0", {"start": v(-25.33, 19.57) * mm, "end": v(-25.89, 18.8) * mm});
            skLineSegment(sketch, "E28.9.6.0", {"start": v(-23.48, 18.67) * mm, "end": v(-25.33, 19.57) * mm});
            skLineSegment(sketch, "E28.1.7.0", {"start": v(-27.3, 12.45) * mm, "end": v(-28.94, 13.69) * mm});
            skLineSegment(sketch, "E28.3.7.0", {"start": v(-28.94, 13.69) * mm, "end": v(-28.51, 14.53) * mm});
            skLineSegment(sketch, "E28.6.7.0", {"start": v(-28.08, 15.37) * mm, "end": v(-28.51, 14.53) * mm});
            skLineSegment(sketch, "E28.9.7.0", {"start": v(-26.11, 14.77) * mm, "end": v(-28.08, 15.37) * mm});
            skLineSegment(sketch, "E28.1.8.0", {"start": v(-28.9, 8.03) * mm, "end": v(-30.73, 9) * mm});
            skLineSegment(sketch, "E28.3.8.0", {"start": v(-30.73, 9) * mm, "end": v(-30.43, 9.89) * mm});
            skLineSegment(sketch, "E28.6.8.0", {"start": v(-30.14, 10.78) * mm, "end": v(-30.43, 9.89) * mm});
            skLineSegment(sketch, "E28.9.8.0", {"start": v(-28.1, 10.5) * mm, "end": v(-30.14, 10.78) * mm});
            skLineSegment(sketch, "E28.1.9.0", {"start": v(-29.8, 3.4) * mm, "end": v(-31.75, 4.08) * mm});
            skLineSegment(sketch, "E28.3.9.0", {"start": v(-31.75, 4.08) * mm, "end": v(-31.6, 5) * mm});
            skLineSegment(sketch, "E28.6.9.0", {"start": v(-31.46, 5.94) * mm, "end": v(-31.6, 5) * mm});
            skLineSegment(sketch, "E28.9.9.0", {"start": v(-29.4, 5.97) * mm, "end": v(-31.46, 5.94) * mm});
            skLineSegment(sketch, "E28.1.10.0", {"start": v(-29.97, -1.3) * mm, "end": v(-32, -0.94) * mm});
            skLineSegment(sketch, "E28.3.10.0", {"start": v(-32, -0.94) * mm, "end": v(-32, 0) * mm});
            skLineSegment(sketch, "E28.6.10.0", {"start": v(-32, 0.94) * mm, "end": v(-32, 0) * mm});
            skLineSegment(sketch, "E28.9.10.0", {"start": v(-29.97, 1.3) * mm, "end": v(-32, 0.94) * mm});
            skLineSegment(sketch, "E28.1.11.0", {"start": v(-29.4, -5.97) * mm, "end": v(-31.46, -5.94) * mm});
            skLineSegment(sketch, "E28.3.11.0", {"start": v(-31.46, -5.94) * mm, "end": v(-31.6, -5) * mm});
            skLineSegment(sketch, "E28.6.11.0", {"start": v(-31.75, -4.08) * mm, "end": v(-31.6, -5) * mm});
            skLineSegment(sketch, "E28.9.11.0", {"start": v(-29.8, -3.4) * mm, "end": v(-31.75, -4.08) * mm});
            skLineSegment(sketch, "E28.1.12.0", {"start": v(-28.1, -10.5) * mm, "end": v(-30.14, -10.78) * mm});
            skLineSegment(sketch, "E28.3.12.0", {"start": v(-30.14, -10.78) * mm, "end": v(-30.43, -9.89) * mm});
            skLineSegment(sketch, "E28.6.12.0", {"start": v(-30.73, -9) * mm, "end": v(-30.43, -9.89) * mm});
            skLineSegment(sketch, "E28.9.12.0", {"start": v(-28.9, -8.03) * mm, "end": v(-30.73, -9) * mm});
            skLineSegment(sketch, "E28.1.13.0", {"start": v(-26.11, -14.77) * mm, "end": v(-28.08, -15.37) * mm});
            skLineSegment(sketch, "E28.3.13.0", {"start": v(-28.08, -15.37) * mm, "end": v(-28.51, -14.53) * mm});
            skLineSegment(sketch, "E28.6.13.0", {"start": v(-28.94, -13.69) * mm, "end": v(-28.51, -14.53) * mm});
            skLineSegment(sketch, "E28.9.13.0", {"start": v(-27.3, -12.45) * mm, "end": v(-28.94, -13.69) * mm});
            skLineSegment(sketch, "E28.1.14.0", {"start": v(-23.48, -18.67) * mm, "end": v(-25.33, -19.57) * mm});
            skLineSegment(sketch, "E28.3.14.0", {"start": v(-25.33, -19.57) * mm, "end": v(-25.89, -18.8) * mm});
            skLineSegment(sketch, "E28.6.14.0", {"start": v(-26.44, -18.05) * mm, "end": v(-25.89, -18.8) * mm});
            skLineSegment(sketch, "E28.9.14.0", {"start": v(-25.01, -16.57) * mm, "end": v(-26.44, -18.05) * mm});
            skLineSegment(sketch, "E28.1.15.0", {"start": v(-20.27, -22.11) * mm, "end": v(-21.96, -23.3) * mm});
            skLineSegment(sketch, "E28.3.15.0", {"start": v(-21.96, -23.3) * mm, "end": v(-22.63, -22.63) * mm});
            skLineSegment(sketch, "E28.6.15.0", {"start": v(-23.3, -21.96) * mm, "end": v(-22.63, -22.63) * mm});
            skLineSegment(sketch, "E28.9.15.0", {"start": v(-22.11, -20.27) * mm, "end": v(-23.3, -21.96) * mm});
            skLineSegment(sketch, "E28.1.16.0", {"start": v(-16.57, -25.01) * mm, "end": v(-18.05, -26.44) * mm});
            skLineSegment(sketch, "E28.3.16.0", {"start": v(-18.05, -26.44) * mm, "end": v(-18.8, -25.89) * mm});
            skLineSegment(sketch, "E28.6.16.0", {"start": v(-19.57, -25.33) * mm, "end": v(-18.8, -25.89) * mm});
            skLineSegment(sketch, "E28.9.16.0", {"start": v(-18.67, -23.48) * mm, "end": v(-19.57, -25.33) * mm});
            skLineSegment(sketch, "E28.1.17.0", {"start": v(-12.45, -27.3) * mm, "end": v(-13.69, -28.94) * mm});
            skLineSegment(sketch, "E28.3.17.0", {"start": v(-13.69, -28.94) * mm, "end": v(-14.53, -28.51) * mm});
            skLineSegment(sketch, "E28.6.17.0", {"start": v(-15.37, -28.08) * mm, "end": v(-14.53, -28.51) * mm});
            skLineSegment(sketch, "E28.9.17.0", {"start": v(-14.77, -26.11) * mm, "end": v(-15.37, -28.08) * mm});
            skLineSegment(sketch, "E28.1.18.0", {"start": v(-8.03, -28.9) * mm, "end": v(-9, -30.73) * mm});
            skLineSegment(sketch, "E28.3.18.0", {"start": v(-9, -30.73) * mm, "end": v(-9.89, -30.43) * mm});
            skLineSegment(sketch, "E28.6.18.0", {"start": v(-10.78, -30.14) * mm, "end": v(-9.89, -30.43) * mm});
            skLineSegment(sketch, "E28.9.18.0", {"start": v(-10.5, -28.1) * mm, "end": v(-10.78, -30.14) * mm});
            skLineSegment(sketch, "E28.1.19.0", {"start": v(-3.4, -29.8) * mm, "end": v(-4.08, -31.75) * mm});
            skLineSegment(sketch, "E28.3.19.0", {"start": v(-4.08, -31.75) * mm, "end": v(-5, -31.6) * mm});
            skLineSegment(sketch, "E28.6.19.0", {"start": v(-5.94, -31.46) * mm, "end": v(-5, -31.6) * mm});
            skLineSegment(sketch, "E28.9.19.0", {"start": v(-5.97, -29.4) * mm, "end": v(-5.94, -31.46) * mm});
            skLineSegment(sketch, "E28.1.20.0", {"start": v(1.3, -29.97) * mm, "end": v(0.94, -32) * mm});
            skLineSegment(sketch, "E28.3.20.0", {"start": v(0.94, -32) * mm, "end": v(0, -32) * mm});
            skLineSegment(sketch, "E28.6.20.0", {"start": v(-0.94, -32) * mm, "end": v(0, -32) * mm});
            skLineSegment(sketch, "E28.9.20.0", {"start": v(-1.3, -29.97) * mm, "end": v(-0.94, -32) * mm});
            skLineSegment(sketch, "E28.1.21.0", {"start": v(5.97, -29.4) * mm, "end": v(5.94, -31.46) * mm});
            skLineSegment(sketch, "E28.3.21.0", {"start": v(5.94, -31.46) * mm, "end": v(5, -31.6) * mm});
            skLineSegment(sketch, "E28.6.21.0", {"start": v(4.08, -31.75) * mm, "end": v(5, -31.6) * mm});
            skLineSegment(sketch, "E28.9.21.0", {"start": v(3.4, -29.8) * mm, "end": v(4.08, -31.75) * mm});
            skLineSegment(sketch, "E28.1.22.0", {"start": v(10.5, -28.1) * mm, "end": v(10.78, -30.14) * mm});
            skLineSegment(sketch, "E28.3.22.0", {"start": v(10.78, -30.14) * mm, "end": v(9.89, -30.43) * mm});
            skLineSegment(sketch, "E28.6.22.0", {"start": v(9, -30.73) * mm, "end": v(9.89, -30.43) * mm});
            skLineSegment(sketch, "E28.9.22.0", {"start": v(8.03, -28.9) * mm, "end": v(9, -30.73) * mm});
            skLineSegment(sketch, "E28.1.23.0", {"start": v(14.77, -26.11) * mm, "end": v(15.37, -28.08) * mm});
            skLineSegment(sketch, "E28.3.23.0", {"start": v(15.37, -28.08) * mm, "end": v(14.53, -28.51) * mm});
            skLineSegment(sketch, "E28.6.23.0", {"start": v(13.69, -28.94) * mm, "end": v(14.53, -28.51) * mm});
            skLineSegment(sketch, "E28.9.23.0", {"start": v(12.45, -27.3) * mm, "end": v(13.69, -28.94) * mm});
            skLineSegment(sketch, "E28.1.24.0", {"start": v(18.67, -23.48) * mm, "end": v(19.57, -25.33) * mm});
            skLineSegment(sketch, "E28.3.24.0", {"start": v(19.57, -25.33) * mm, "end": v(18.8, -25.89) * mm});
            skLineSegment(sketch, "E28.6.24.0", {"start": v(18.05, -26.44) * mm, "end": v(18.8, -25.89) * mm});
            skLineSegment(sketch, "E28.9.24.0", {"start": v(16.57, -25.01) * mm, "end": v(18.05, -26.44) * mm});
            skLineSegment(sketch, "E28.1.25.0", {"start": v(22.11, -20.27) * mm, "end": v(23.3, -21.96) * mm});
            skLineSegment(sketch, "E28.3.25.0", {"start": v(23.3, -21.96) * mm, "end": v(22.63, -22.63) * mm});
            skLineSegment(sketch, "E28.6.25.0", {"start": v(21.96, -23.3) * mm, "end": v(22.63, -22.63) * mm});
            skLineSegment(sketch, "E28.9.25.0", {"start": v(20.27, -22.11) * mm, "end": v(21.96, -23.3) * mm});
            skLineSegment(sketch, "E28.1.26.0", {"start": v(25.01, -16.57) * mm, "end": v(26.44, -18.05) * mm});
            skLineSegment(sketch, "E28.3.26.0", {"start": v(26.44, -18.05) * mm, "end": v(25.89, -18.8) * mm});
            skLineSegment(sketch, "E28.6.26.0", {"start": v(25.33, -19.57) * mm, "end": v(25.89, -18.8) * mm});
            skLineSegment(sketch, "E28.9.26.0", {"start": v(23.48, -18.67) * mm, "end": v(25.33, -19.57) * mm});
            skLineSegment(sketch, "E28.1.27.0", {"start": v(27.3, -12.45) * mm, "end": v(28.94, -13.69) * mm});
            skLineSegment(sketch, "E28.3.27.0", {"start": v(28.94, -13.69) * mm, "end": v(28.51, -14.53) * mm});
            skLineSegment(sketch, "E28.6.27.0", {"start": v(28.08, -15.37) * mm, "end": v(28.51, -14.53) * mm});
            skLineSegment(sketch, "E28.9.27.0", {"start": v(26.11, -14.77) * mm, "end": v(28.08, -15.37) * mm});
            skLineSegment(sketch, "E28.1.28.0", {"start": v(28.9, -8.03) * mm, "end": v(30.73, -9) * mm});
            skLineSegment(sketch, "E28.3.28.0", {"start": v(30.73, -9) * mm, "end": v(30.43, -9.89) * mm});
            skLineSegment(sketch, "E28.6.28.0", {"start": v(30.14, -10.78) * mm, "end": v(30.43, -9.89) * mm});
            skLineSegment(sketch, "E28.9.28.0", {"start": v(28.1, -10.5) * mm, "end": v(30.14, -10.78) * mm});
            skLineSegment(sketch, "E28.1.29.0", {"start": v(29.8, -3.4) * mm, "end": v(31.75, -4.08) * mm});
            skLineSegment(sketch, "E28.3.29.0", {"start": v(31.75, -4.08) * mm, "end": v(31.6, -5) * mm});
            skLineSegment(sketch, "E28.6.29.0", {"start": v(31.46, -5.94) * mm, "end": v(31.6, -5) * mm});
            skLineSegment(sketch, "E28.9.29.0", {"start": v(29.4, -5.97) * mm, "end": v(31.46, -5.94) * mm});
            skLineSegment(sketch, "E28.1.30.0", {"start": v(29.97, 1.3) * mm, "end": v(32, 0.94) * mm});
            skLineSegment(sketch, "E28.3.30.0", {"start": v(32, 0.94) * mm, "end": v(32, 0) * mm});
            skLineSegment(sketch, "E28.6.30.0", {"start": v(32, -0.94) * mm, "end": v(32, 0) * mm});
            skLineSegment(sketch, "E28.9.30.0", {"start": v(29.97, -1.3) * mm, "end": v(32, -0.94) * mm});
            skLineSegment(sketch, "E28.1.31.0", {"start": v(29.4, 5.97) * mm, "end": v(31.46, 5.94) * mm});
            skLineSegment(sketch, "E28.3.31.0", {"start": v(31.46, 5.94) * mm, "end": v(31.6, 5) * mm});
            skLineSegment(sketch, "E28.6.31.0", {"start": v(31.75, 4.08) * mm, "end": v(31.6, 5) * mm});
            skLineSegment(sketch, "E28.9.31.0", {"start": v(29.8, 3.4) * mm, "end": v(31.75, 4.08) * mm});
            skLineSegment(sketch, "E28.1.32.0", {"start": v(28.1, 10.5) * mm, "end": v(30.14, 10.78) * mm});
            skLineSegment(sketch, "E28.3.32.0", {"start": v(30.14, 10.78) * mm, "end": v(30.43, 9.89) * mm});
            skLineSegment(sketch, "E28.6.32.0", {"start": v(30.73, 9) * mm, "end": v(30.43, 9.89) * mm});
            skLineSegment(sketch, "E28.9.32.0", {"start": v(28.9, 8.03) * mm, "end": v(30.73, 9) * mm});
            skLineSegment(sketch, "E28.1.33.0", {"start": v(26.11, 14.77) * mm, "end": v(28.08, 15.37) * mm});
            skLineSegment(sketch, "E28.3.33.0", {"start": v(28.08, 15.37) * mm, "end": v(28.51, 14.53) * mm});
            skLineSegment(sketch, "E28.6.33.0", {"start": v(28.94, 13.69) * mm, "end": v(28.51, 14.53) * mm});
            skLineSegment(sketch, "E28.9.33.0", {"start": v(27.3, 12.45) * mm, "end": v(28.94, 13.69) * mm});
            skLineSegment(sketch, "E28.1.34.0", {"start": v(23.48, 18.67) * mm, "end": v(25.33, 19.57) * mm});
            skLineSegment(sketch, "E28.3.34.0", {"start": v(25.33, 19.57) * mm, "end": v(25.89, 18.8) * mm});
            skLineSegment(sketch, "E28.6.34.0", {"start": v(26.44, 18.05) * mm, "end": v(25.89, 18.8) * mm});
            skLineSegment(sketch, "E28.9.34.0", {"start": v(25.01, 16.57) * mm, "end": v(26.44, 18.05) * mm});
            skLineSegment(sketch, "E28.1.35.0", {"start": v(20.27, 22.11) * mm, "end": v(21.96, 23.3) * mm});
            skLineSegment(sketch, "E28.3.35.0", {"start": v(21.96, 23.3) * mm, "end": v(22.63, 22.63) * mm});
            skLineSegment(sketch, "E28.6.35.0", {"start": v(23.3, 21.96) * mm, "end": v(22.63, 22.63) * mm});
            skLineSegment(sketch, "E28.9.35.0", {"start": v(22.11, 20.27) * mm, "end": v(23.3, 21.96) * mm});
            skLineSegment(sketch, "E28.1.36.0", {"start": v(16.57, 25.01) * mm, "end": v(18.05, 26.44) * mm});
            skLineSegment(sketch, "E28.3.36.0", {"start": v(18.05, 26.44) * mm, "end": v(18.8, 25.89) * mm});
            skLineSegment(sketch, "E28.6.36.0", {"start": v(19.57, 25.33) * mm, "end": v(18.8, 25.89) * mm});
            skLineSegment(sketch, "E28.9.36.0", {"start": v(18.67, 23.48) * mm, "end": v(19.57, 25.33) * mm});
            skLineSegment(sketch, "E28.1.37.0", {"start": v(12.45, 27.3) * mm, "end": v(13.69, 28.94) * mm});
            skLineSegment(sketch, "E28.3.37.0", {"start": v(13.69, 28.94) * mm, "end": v(14.53, 28.51) * mm});
            skLineSegment(sketch, "E28.6.37.0", {"start": v(15.37, 28.08) * mm, "end": v(14.53, 28.51) * mm});
            skLineSegment(sketch, "E28.9.37.0", {"start": v(14.77, 26.11) * mm, "end": v(15.37, 28.08) * mm});
            skLineSegment(sketch, "E28.1.38.0", {"start": v(8.03, 28.9) * mm, "end": v(9, 30.73) * mm});
            skLineSegment(sketch, "E28.3.38.0", {"start": v(9, 30.73) * mm, "end": v(9.89, 30.43) * mm});
            skLineSegment(sketch, "E28.6.38.0", {"start": v(10.78, 30.14) * mm, "end": v(9.89, 30.43) * mm});
            skLineSegment(sketch, "E28.9.38.0", {"start": v(10.5, 28.1) * mm, "end": v(10.78, 30.14) * mm});
            skLineSegment(sketch, "E28.1.39.0", {"start": v(3.4, 29.8) * mm, "end": v(4.08, 31.75) * mm});
            skLineSegment(sketch, "E28.3.39.0", {"start": v(4.08, 31.75) * mm, "end": v(5, 31.6) * mm});
            skLineSegment(sketch, "E28.6.39.0", {"start": v(5.94, 31.46) * mm, "end": v(5, 31.6) * mm});
            skLineSegment(sketch, "E28.9.39.0", {"start": v(5.97, 29.4) * mm, "end": v(5.94, 31.46) * mm});
            skSolve(sketch);
        }
        {
            var Q0;
            Q0 = qSketchRegion(id + "F14", true);
            extrude(context, id + "F15", {"entities" : qUnion([Q0]), "operationType" : NewBodyOperationType.ADD, "depth" : 4 * mm, "offsetDistance" : 25 * mm});
        }
        {
            var Q0;
            Q0=makeQuery(id+"F7.opExtrude","CAP_FACE",FACE,{"disambiguationData":[OSD([sQuery(id+"F0.wireOp",EDGE,"E0")])],"isStart":false});
            var sketch = newSketch(context, id + "F16", { "sketchPlane" : qUnion([Q0])});
            skCircle(sketch, "E29", {"center": v(40, 0) * mm, "radius": 7.5 * mm});
            skLineSegment(sketch, "E30", {"start": v(40, 0) * mm, "end": v(40, 7.5) * mm, "construction": true});
            skLineSegment(sketch, "E31", {"start": v(38.68, 7.38) * mm, "end": v(39.06, 9.5) * mm});
            skLineSegment(sketch, "E32", {"start": v(39.06, 9.5) * mm, "end": v(40.94, 9.5) * mm});
            skLineSegment(sketch, "E33.MirrorCS", {"start": v(41.32, 7.38) * mm, "end": v(40.94, 9.5) * mm});
            skLineSegment(sketch, "E34.1.0", {"start": v(33.65, 7.13) * mm, "end": v(35.18, 8.24) * mm});
            skLineSegment(sketch, "E34.1.1", {"start": v(34.6, 5.2) * mm, "end": v(33.65, 7.13) * mm});
            skLineSegment(sketch, "E34.1.2", {"start": v(36.72, 6.75) * mm, "end": v(35.18, 8.24) * mm});
            skLineSegment(sketch, "E34.2.0", {"start": v(30.67, 2.04) * mm, "end": v(31.26, 3.83) * mm});
            skLineSegment(sketch, "E34.2.1", {"start": v(32.57, 1.03) * mm, "end": v(30.67, 2.04) * mm});
            skLineSegment(sketch, "E34.2.2", {"start": v(33.38, 3.53) * mm, "end": v(31.26, 3.83) * mm});
            skLineSegment(sketch, "E35.1.3.0", {"start": v(31.26, -3.83) * mm, "end": v(30.67, -2.04) * mm});
            skLineSegment(sketch, "E35.3.3.0", {"start": v(33.38, -3.53) * mm, "end": v(31.26, -3.83) * mm});
            skLineSegment(sketch, "E35.6.3.0", {"start": v(32.57, -1.03) * mm, "end": v(30.67, -2.04) * mm});
            skLineSegment(sketch, "E35.1.4.0", {"start": v(35.18, -8.24) * mm, "end": v(33.65, -7.13) * mm});
            skLineSegment(sketch, "E35.3.4.0", {"start": v(36.72, -6.75) * mm, "end": v(35.18, -8.24) * mm});
            skLineSegment(sketch, "E35.6.4.0", {"start": v(34.6, -5.2) * mm, "end": v(33.65, -7.13) * mm});
            skLineSegment(sketch, "E35.1.5.0", {"start": v(40.94, -9.5) * mm, "end": v(39.06, -9.5) * mm});
            skLineSegment(sketch, "E35.3.5.0", {"start": v(41.32, -7.38) * mm, "end": v(40.94, -9.5) * mm});
            skLineSegment(sketch, "E35.6.5.0", {"start": v(38.68, -7.38) * mm, "end": v(39.06, -9.5) * mm});
            skLineSegment(sketch, "E35.1.6.0", {"start": v(46.35, -7.13) * mm, "end": v(44.82, -8.24) * mm});
            skLineSegment(sketch, "E35.3.6.0", {"start": v(45.4, -5.2) * mm, "end": v(46.35, -7.13) * mm});
            skLineSegment(sketch, "E35.6.6.0", {"start": v(43.28, -6.75) * mm, "end": v(44.82, -8.24) * mm});
            skLineSegment(sketch, "E35.1.7.0", {"start": v(49.33, -2.04) * mm, "end": v(48.74, -3.83) * mm});
            skLineSegment(sketch, "E35.3.7.0", {"start": v(47.43, -1.03) * mm, "end": v(49.33, -2.04) * mm});
            skLineSegment(sketch, "E35.6.7.0", {"start": v(46.62, -3.53) * mm, "end": v(48.74, -3.83) * mm});
            skLineSegment(sketch, "E35.1.8.0", {"start": v(48.74, 3.83) * mm, "end": v(49.33, 2.04) * mm});
            skLineSegment(sketch, "E35.3.8.0", {"start": v(46.62, 3.53) * mm, "end": v(48.74, 3.83) * mm});
            skLineSegment(sketch, "E35.6.8.0", {"start": v(47.43, 1.03) * mm, "end": v(49.33, 2.04) * mm});
            skLineSegment(sketch, "E35.1.9.0", {"start": v(44.82, 8.24) * mm, "end": v(46.35, 7.13) * mm});
            skLineSegment(sketch, "E35.3.9.0", {"start": v(43.28, 6.75) * mm, "end": v(44.82, 8.24) * mm});
            skLineSegment(sketch, "E35.6.9.0", {"start": v(45.4, 5.2) * mm, "end": v(46.35, 7.13) * mm});
            skSolve(sketch);
        }
        {
            var Q0;
            Q0 = qSketchRegion(id + "F16", true);
            extrude(context, id + "F17", {"entities" : qUnion([Q0]), "operationType" : NewBodyOperationType.ADD, "depth" : 4 * mm, "offsetDistance" : 25 * mm});
        }
        {
            var Q0;
            Q0=makeQuery(id+"F17.opExtrude","CAP_FACE",FACE,{"disambiguationData":[OSD([sQuery(id+"F16.wireOp",EDGE,"E29"),sQuery(id+"F16.wireOp",EDGE,"E31"),sQuery(id+"F16.wireOp",EDGE,"E32"),sQuery(id+"F16.wireOp",EDGE,"E33.MirrorCS"),sQuery(id+"F16.wireOp",EDGE,"E34.1.0"),sQuery(id+"F16.wireOp",EDGE,"E34.1.1"),sQuery(id+"F16.wireOp",EDGE,"E34.1.2"),sQuery(id+"F16.wireOp",EDGE,"E34.2.0"),sQuery(id+"F16.wireOp",EDGE,"E34.2.1"),sQuery(id+"F16.wireOp",EDGE,"E34.2.2"),sQuery(id+"F16.wireOp",EDGE,"E35.1.3.0"),sQuery(id+"F16.wireOp",EDGE,"E35.3.3.0"),sQuery(id+"F16.wireOp",EDGE,"E35.6.3.0"),sQuery(id+"F16.wireOp",EDGE,"E35.1.4.0"),sQuery(id+"F16.wireOp",EDGE,"E35.3.4.0"),sQuery(id+"F16.wireOp",EDGE,"E35.6.4.0"),sQuery(id+"F16.wireOp",EDGE,"E35.1.5.0"),sQuery(id+"F16.wireOp",EDGE,"E35.3.5.0"),sQuery(id+"F16.wireOp",EDGE,"E35.6.5.0"),sQuery(id+"F16.wireOp",EDGE,"E35.1.6.0"),sQuery(id+"F16.wireOp",EDGE,"E35.3.6.0"),sQuery(id+"F16.wireOp",EDGE,"E35.6.6.0"),sQuery(id+"F16.wireOp",EDGE,"E35.1.7.0"),sQuery(id+"F16.wireOp",EDGE,"E35.3.7.0"),sQuery(id+"F16.wireOp",EDGE,"E35.6.7.0"),sQuery(id+"F16.wireOp",EDGE,"E35.1.8.0"),sQuery(id+"F16.wireOp",EDGE,"E35.3.8.0"),sQuery(id+"F16.wireOp",EDGE,"E35.6.8.0"),sQuery(id+"F16.wireOp",EDGE,"E35.1.9.0"),sQuery(id+"F16.wireOp",EDGE,"E35.3.9.0"),sQuery(id+"F16.wireOp",EDGE,"E35.6.9.0")])],"isStart":false});
            var sketch = newSketch(context, id + "F18", { "sketchPlane" : qUnion([Q0])});
            skCircle(sketch, "E36.0", {"center": v(40, 0) * mm, "radius": 3 * mm});
            skSolve(sketch);
        }
        {
            var Q0;
            Q0 = qSketchRegion(id + "F18", true);
            extrude(context, id + "F19", {"entities" : qUnion([Q0]), "operationType" : NewBodyOperationType.ADD, "depth" : 2 * mm, "offsetDistance" : 25 * mm});
        }
        {
            var Q0;
            Q0=makeQuery(id+"F19.opExtrude","CAP_FACE",FACE,{"disambiguationData":[OSD([sQuery(id+"F18.wireOp",EDGE,"E36.0")])],"isStart":false});
            var sketch = newSketch(context, id + "F20", { "sketchPlane" : qUnion([Q0])});
            skCircle(sketch, "E37", {"center": v(0, 0) * mm, "radius": 98 * mm});
            skCircle(sketch, "E38.0", {"center": v(0, 0) * mm, "radius": 5 * mm});
            skSolve(sketch);
        }
        {
            var Q0;
            Q0 = qSketchRegion(id + "F20", true);
            extrude(context, id + "F21", {"entities" : qUnion([Q0]), "depth" : 1 * mm, "offsetDistance" : 25 * mm});
        }
        {
            var Q0;
            Q0=makeQuery(id+"F21.opExtrude","SWEPT_BODY",BODY,{"disambiguationData":[OSD([sQuery(id+"F20.wireOp",EDGE,"E37"),sQuery(id+"F20.wireOp",EDGE,"E38.0")])]});
            var Q1;
            Q1=makeQuery(id+"F1.opExtrude","SWEPT_BODY",BODY,{"disambiguationData":[OSD([sQuery(id+"F0.wireOp",EDGE,"E0")])]});
            booleanBodies(context, id + "F22", {"operationType" : BooleanOperationType.SUBTRACTION, "tools" : qUnion([Q0]), "targets" : qUnion([Q1]), "keepTools" : true});
        }
        {
            var Q0;
            Q0=makeQuery(id+"F21.opExtrude","CAP_FACE",FACE,{"disambiguationData":[OSD([sQuery(id+"F20.wireOp",EDGE,"E37"),sQuery(id+"F20.wireOp",EDGE,"E38.0")])],"isStart":true});
            var sketch = newSketch(context, id + "F23", { "sketchPlane" : qUnion([Q0])});
            skCircle(sketch, "E39.0", {"center": v(-40, 0) * mm, "radius": 3 * mm});
            skCircle(sketch, "E40", {"center": v(-40, 0) * mm, "radius": 5 * mm});
            skSolve(sketch);
        }
        {
            var Q0;
            Q0 = qSketchRegion(id + "F23", true);
            extrude(context, id + "F24", {"entities" : qUnion([Q0]), "operationType" : NewBodyOperationType.ADD, "endBound" : BoundingType.UP_TO_NEXT, "depth" : 2 * mm, "offsetDistance" : 25 * mm});
        }
        {
            var Q0;
            Q0=makeQuery(id+"F21.opExtrude","CAP_FACE",FACE,{"disambiguationData":[OSD([sQuery(id+"F20.wireOp",EDGE,"E37"),sQuery(id+"F20.wireOp",EDGE,"E38.0")])],"isStart":false});
            var sketch = newSketch(context, id + "F25", { "sketchPlane" : qUnion([Q0])});
            skLineSegment(sketch, "E41.bottom", {"start": v(1.5, 71) * mm, "end": v(-1.5, 71) * mm});
            skLineSegment(sketch, "E41.top", {"start": v(1.5, 91) * mm, "end": v(-1.5, 91) * mm});
            skLineSegment(sketch, "E41.left", {"start": v(1.5, 71) * mm, "end": v(1.5, 91) * mm});
            skLineSegment(sketch, "E41.right", {"start": v(-1.5, 71) * mm, "end": v(-1.5, 91) * mm});
            skPoint(sketch, "E41.middle", {"position": v(0, 81) * mm});
            skLineSegment(sketch, "E42.1.0", {"start": v(-34.2, 62.24) * mm, "end": v(-44.2, 79.56) * mm});
            skLineSegment(sketch, "E42.1.1", {"start": v(-44.2, 79.56) * mm, "end": v(-46.8, 78.06) * mm});
            skLineSegment(sketch, "E42.1.2", {"start": v(-36.8, 60.74) * mm, "end": v(-46.8, 78.06) * mm});
            skLineSegment(sketch, "E42.1.3", {"start": v(-34.2, 62.24) * mm, "end": v(-36.8, 60.74) * mm});
            skLineSegment(sketch, "E42.2.0", {"start": v(-60.74, 36.8) * mm, "end": v(-78.06, 46.8) * mm});
            skLineSegment(sketch, "E42.2.1", {"start": v(-78.06, 46.8) * mm, "end": v(-79.56, 44.2) * mm});
            skLineSegment(sketch, "E42.2.2", {"start": v(-62.24, 34.2) * mm, "end": v(-79.56, 44.2) * mm});
            skLineSegment(sketch, "E42.2.3", {"start": v(-60.74, 36.8) * mm, "end": v(-62.24, 34.2) * mm});
            skPoint(sketch, "E42.center", {"position": v(0, 0) * mm});
            skLineSegment(sketch, "E43.1.3.0", {"start": v(-71, 1.5) * mm, "end": v(-91, 1.5) * mm});
            skLineSegment(sketch, "E43.3.3.0", {"start": v(-91, 1.5) * mm, "end": v(-91, -1.5) * mm});
            skLineSegment(sketch, "E43.6.3.0", {"start": v(-71, -1.5) * mm, "end": v(-91, -1.5) * mm});
            skLineSegment(sketch, "E43.9.3.0", {"start": v(-71, 1.5) * mm, "end": v(-71, -1.5) * mm});
            skLineSegment(sketch, "E43.1.4.0", {"start": v(-62.24, -34.2) * mm, "end": v(-79.56, -44.2) * mm});
            skLineSegment(sketch, "E43.3.4.0", {"start": v(-79.56, -44.2) * mm, "end": v(-78.06, -46.8) * mm});
            skLineSegment(sketch, "E43.6.4.0", {"start": v(-60.74, -36.8) * mm, "end": v(-78.06, -46.8) * mm});
            skLineSegment(sketch, "E43.9.4.0", {"start": v(-62.24, -34.2) * mm, "end": v(-60.74, -36.8) * mm});
            skLineSegment(sketch, "E43.1.5.0", {"start": v(-36.8, -60.74) * mm, "end": v(-46.8, -78.06) * mm});
            skLineSegment(sketch, "E43.3.5.0", {"start": v(-46.8, -78.06) * mm, "end": v(-44.2, -79.56) * mm});
            skLineSegment(sketch, "E43.6.5.0", {"start": v(-34.2, -62.24) * mm, "end": v(-44.2, -79.56) * mm});
            skLineSegment(sketch, "E43.9.5.0", {"start": v(-36.8, -60.74) * mm, "end": v(-34.2, -62.24) * mm});
            skLineSegment(sketch, "E43.1.6.0", {"start": v(-1.5, -71) * mm, "end": v(-1.5, -91) * mm});
            skLineSegment(sketch, "E43.3.6.0", {"start": v(-1.5, -91) * mm, "end": v(1.5, -91) * mm});
            skLineSegment(sketch, "E43.6.6.0", {"start": v(1.5, -71) * mm, "end": v(1.5, -91) * mm});
            skLineSegment(sketch, "E43.9.6.0", {"start": v(-1.5, -71) * mm, "end": v(1.5, -71) * mm});
            skLineSegment(sketch, "E43.1.7.0", {"start": v(34.2, -62.24) * mm, "end": v(44.2, -79.56) * mm});
            skLineSegment(sketch, "E43.3.7.0", {"start": v(44.2, -79.56) * mm, "end": v(46.8, -78.06) * mm});
            skLineSegment(sketch, "E43.6.7.0", {"start": v(36.8, -60.74) * mm, "end": v(46.8, -78.06) * mm});
            skLineSegment(sketch, "E43.9.7.0", {"start": v(34.2, -62.24) * mm, "end": v(36.8, -60.74) * mm});
            skLineSegment(sketch, "E43.1.8.0", {"start": v(60.74, -36.8) * mm, "end": v(78.06, -46.8) * mm});
            skLineSegment(sketch, "E43.3.8.0", {"start": v(78.06, -46.8) * mm, "end": v(79.56, -44.2) * mm});
            skLineSegment(sketch, "E43.6.8.0", {"start": v(62.24, -34.2) * mm, "end": v(79.56, -44.2) * mm});
            skLineSegment(sketch, "E43.9.8.0", {"start": v(60.74, -36.8) * mm, "end": v(62.24, -34.2) * mm});
            skLineSegment(sketch, "E43.1.9.0", {"start": v(71, -1.5) * mm, "end": v(91, -1.5) * mm});
            skLineSegment(sketch, "E43.3.9.0", {"start": v(91, -1.5) * mm, "end": v(91, 1.5) * mm});
            skLineSegment(sketch, "E43.6.9.0", {"start": v(71, 1.5) * mm, "end": v(91, 1.5) * mm});
            skLineSegment(sketch, "E43.9.9.0", {"start": v(71, -1.5) * mm, "end": v(71, 1.5) * mm});
            skLineSegment(sketch, "E43.1.10.0", {"start": v(62.24, 34.2) * mm, "end": v(79.56, 44.2) * mm});
            skLineSegment(sketch, "E43.3.10.0", {"start": v(79.56, 44.2) * mm, "end": v(78.06, 46.8) * mm});
            skLineSegment(sketch, "E43.6.10.0", {"start": v(60.74, 36.8) * mm, "end": v(78.06, 46.8) * mm});
            skLineSegment(sketch, "E43.9.10.0", {"start": v(62.24, 34.2) * mm, "end": v(60.74, 36.8) * mm});
            skLineSegment(sketch, "E43.1.11.0", {"start": v(36.8, 60.74) * mm, "end": v(46.8, 78.06) * mm});
            skLineSegment(sketch, "E43.3.11.0", {"start": v(46.8, 78.06) * mm, "end": v(44.2, 79.56) * mm});
            skLineSegment(sketch, "E43.6.11.0", {"start": v(34.2, 62.24) * mm, "end": v(44.2, 79.56) * mm});
            skLineSegment(sketch, "E43.9.11.0", {"start": v(36.8, 60.74) * mm, "end": v(34.2, 62.24) * mm});
            skSolve(sketch);
        }
        {
            var Q0;
            Q0 = qSketchRegion(id + "F25", true);
            extrude(context, id + "F26", {"entities" : qUnion([Q0]), "operationType" : NewBodyOperationType.REMOVE, "oppositeDirection" : true, "depth" : 0.5 * mm, "offsetDistance" : 25 * mm});
        }
        {
            var Q0;
            Q0=makeQuery(id+"F21.opExtrude","CAP_FACE",FACE,{"disambiguationData":[OSD([sQuery(id+"F20.wireOp",EDGE,"E37"),sQuery(id+"F20.wireOp",EDGE,"E38.0")])],"isStart":false});
            var sketch = newSketch(context, id + "F27", { "sketchPlane" : qUnion([Q0])});
            skLineSegment(sketch, "E44.bottom", {"start": v(0.75, 78.5) * mm, "end": v(-0.75, 78.5) * mm});
            skLineSegment(sketch, "E44.top", {"start": v(0.75, 90.5) * mm, "end": v(-0.75, 90.5) * mm});
            skLineSegment(sketch, "E44.left", {"start": v(0.75, 78.5) * mm, "end": v(0.75, 90.5) * mm});
            skLineSegment(sketch, "E44.right", {"start": v(-0.75, 78.5) * mm, "end": v(-0.75, 90.5) * mm});
            skPoint(sketch, "E44.middle", {"position": v(0, 84.5) * mm});
            skLineSegment(sketch, "E45.1.0", {"start": v(-7.46, 78.15) * mm, "end": v(-8.71, 90.08) * mm});
            skLineSegment(sketch, "E45.1.1", {"start": v(-8.71, 90.08) * mm, "end": v(-10.2, 89.93) * mm});
            skLineSegment(sketch, "E45.1.2", {"start": v(-8.95, 78) * mm, "end": v(-10.2, 89.93) * mm});
            skLineSegment(sketch, "E45.1.3", {"start": v(-7.46, 78.15) * mm, "end": v(-8.95, 78) * mm});
            skLineSegment(sketch, "E45.2.0", {"start": v(-15.59, 76.94) * mm, "end": v(-18.08, 88.68) * mm});
            skLineSegment(sketch, "E45.2.1", {"start": v(-18.08, 88.68) * mm, "end": v(-19.55, 88.37) * mm});
            skLineSegment(sketch, "E45.2.2", {"start": v(-17.05, 76.63) * mm, "end": v(-19.55, 88.37) * mm});
            skLineSegment(sketch, "E45.2.3", {"start": v(-15.59, 76.94) * mm, "end": v(-17.05, 76.63) * mm});
            skPoint(sketch, "E45.center", {"position": v(0, 0) * mm});
            skLineSegment(sketch, "E46.1.3.0", {"start": v(-23.54, 74.89) * mm, "end": v(-27.25, 86.3) * mm});
            skLineSegment(sketch, "E46.3.3.0", {"start": v(-27.25, 86.3) * mm, "end": v(-28.68, 85.84) * mm});
            skLineSegment(sketch, "E46.6.3.0", {"start": v(-24.97, 74.43) * mm, "end": v(-28.68, 85.84) * mm});
            skLineSegment(sketch, "E46.9.3.0", {"start": v(-23.54, 74.89) * mm, "end": v(-24.97, 74.43) * mm});
            skLineSegment(sketch, "E46.1.4.0", {"start": v(-31.24, 72.02) * mm, "end": v(-36.12, 82.98) * mm});
            skLineSegment(sketch, "E46.3.4.0", {"start": v(-36.12, 82.98) * mm, "end": v(-37.5, 82.37) * mm});
            skLineSegment(sketch, "E46.6.4.0", {"start": v(-32.61, 71.4) * mm, "end": v(-37.5, 82.37) * mm});
            skLineSegment(sketch, "E46.9.4.0", {"start": v(-31.24, 72.02) * mm, "end": v(-32.61, 71.4) * mm});
            skLineSegment(sketch, "E46.1.5.0", {"start": v(-38.6, 68.36) * mm, "end": v(-44.6, 78.75) * mm});
            skLineSegment(sketch, "E46.3.5.0", {"start": v(-44.6, 78.75) * mm, "end": v(-45.9, 78) * mm});
            skLineSegment(sketch, "E46.6.5.0", {"start": v(-39.9, 67.6) * mm, "end": v(-45.9, 78) * mm});
            skLineSegment(sketch, "E46.9.5.0", {"start": v(-38.6, 68.36) * mm, "end": v(-39.9, 67.6) * mm});
            skLineSegment(sketch, "E46.1.6.0", {"start": v(-45.53, 63.95) * mm, "end": v(-52.59, 73.66) * mm});
            skLineSegment(sketch, "E46.3.6.0", {"start": v(-52.59, 73.66) * mm, "end": v(-53.8, 72.78) * mm});
            skLineSegment(sketch, "E46.6.6.0", {"start": v(-46.75, 63.07) * mm, "end": v(-53.8, 72.78) * mm});
            skLineSegment(sketch, "E46.9.6.0", {"start": v(-45.53, 63.95) * mm, "end": v(-46.75, 63.07) * mm});
            skLineSegment(sketch, "E46.1.7.0", {"start": v(-51.97, 58.84) * mm, "end": v(-60, 67.76) * mm});
            skLineSegment(sketch, "E46.3.7.0", {"start": v(-60, 67.76) * mm, "end": v(-61.11, 66.75) * mm});
            skLineSegment(sketch, "E46.6.7.0", {"start": v(-53.08, 57.84) * mm, "end": v(-61.11, 66.75) * mm});
            skLineSegment(sketch, "E46.9.7.0", {"start": v(-51.97, 58.84) * mm, "end": v(-53.08, 57.84) * mm});
            skLineSegment(sketch, "E46.1.8.0", {"start": v(-57.84, 53.08) * mm, "end": v(-66.75, 61.11) * mm});
            skLineSegment(sketch, "E46.3.8.0", {"start": v(-66.75, 61.11) * mm, "end": v(-67.76, 60) * mm});
            skLineSegment(sketch, "E46.6.8.0", {"start": v(-58.84, 51.97) * mm, "end": v(-67.76, 60) * mm});
            skLineSegment(sketch, "E46.9.8.0", {"start": v(-57.84, 53.08) * mm, "end": v(-58.84, 51.97) * mm});
            skLineSegment(sketch, "E46.1.9.0", {"start": v(-63.07, 46.75) * mm, "end": v(-72.78, 53.8) * mm});
            skLineSegment(sketch, "E46.3.9.0", {"start": v(-72.78, 53.8) * mm, "end": v(-73.66, 52.59) * mm});
            skLineSegment(sketch, "E46.6.9.0", {"start": v(-63.95, 45.53) * mm, "end": v(-73.66, 52.59) * mm});
            skLineSegment(sketch, "E46.9.9.0", {"start": v(-63.07, 46.75) * mm, "end": v(-63.95, 45.53) * mm});
            skLineSegment(sketch, "E46.1.10.0", {"start": v(-67.6, 39.9) * mm, "end": v(-78, 45.9) * mm});
            skLineSegment(sketch, "E46.3.10.0", {"start": v(-78, 45.9) * mm, "end": v(-78.75, 44.6) * mm});
            skLineSegment(sketch, "E46.6.10.0", {"start": v(-68.36, 38.6) * mm, "end": v(-78.75, 44.6) * mm});
            skLineSegment(sketch, "E46.9.10.0", {"start": v(-67.6, 39.9) * mm, "end": v(-68.36, 38.6) * mm});
            skLineSegment(sketch, "E46.1.11.0", {"start": v(-71.4, 32.61) * mm, "end": v(-82.37, 37.5) * mm});
            skLineSegment(sketch, "E46.3.11.0", {"start": v(-82.37, 37.5) * mm, "end": v(-82.98, 36.12) * mm});
            skLineSegment(sketch, "E46.6.11.0", {"start": v(-72.02, 31.24) * mm, "end": v(-82.98, 36.12) * mm});
            skLineSegment(sketch, "E46.9.11.0", {"start": v(-71.4, 32.61) * mm, "end": v(-72.02, 31.24) * mm});
            skLineSegment(sketch, "E46.1.12.0", {"start": v(-74.43, 24.97) * mm, "end": v(-85.84, 28.68) * mm});
            skLineSegment(sketch, "E46.3.12.0", {"start": v(-85.84, 28.68) * mm, "end": v(-86.3, 27.25) * mm});
            skLineSegment(sketch, "E46.6.12.0", {"start": v(-74.89, 23.54) * mm, "end": v(-86.3, 27.25) * mm});
            skLineSegment(sketch, "E46.9.12.0", {"start": v(-74.43, 24.97) * mm, "end": v(-74.89, 23.54) * mm});
            skLineSegment(sketch, "E46.1.13.0", {"start": v(-76.63, 17.05) * mm, "end": v(-88.37, 19.55) * mm});
            skLineSegment(sketch, "E46.3.13.0", {"start": v(-88.37, 19.55) * mm, "end": v(-88.68, 18.08) * mm});
            skLineSegment(sketch, "E46.6.13.0", {"start": v(-76.94, 15.59) * mm, "end": v(-88.68, 18.08) * mm});
            skLineSegment(sketch, "E46.9.13.0", {"start": v(-76.63, 17.05) * mm, "end": v(-76.94, 15.59) * mm});
            skLineSegment(sketch, "E46.1.14.0", {"start": v(-78, 8.95) * mm, "end": v(-89.93, 10.2) * mm});
            skLineSegment(sketch, "E46.3.14.0", {"start": v(-89.93, 10.2) * mm, "end": v(-90.08, 8.71) * mm});
            skLineSegment(sketch, "E46.6.14.0", {"start": v(-78.15, 7.46) * mm, "end": v(-90.08, 8.71) * mm});
            skLineSegment(sketch, "E46.9.14.0", {"start": v(-78, 8.95) * mm, "end": v(-78.15, 7.46) * mm});
            skLineSegment(sketch, "E46.1.15.0", {"start": v(-78.5, 0.75) * mm, "end": v(-90.5, 0.75) * mm});
            skLineSegment(sketch, "E46.3.15.0", {"start": v(-90.5, 0.75) * mm, "end": v(-90.5, -0.75) * mm});
            skLineSegment(sketch, "E46.6.15.0", {"start": v(-78.5, -0.75) * mm, "end": v(-90.5, -0.75) * mm});
            skLineSegment(sketch, "E46.9.15.0", {"start": v(-78.5, 0.75) * mm, "end": v(-78.5, -0.75) * mm});
            skLineSegment(sketch, "E46.1.16.0", {"start": v(-78.15, -7.46) * mm, "end": v(-90.08, -8.71) * mm});
            skLineSegment(sketch, "E46.3.16.0", {"start": v(-90.08, -8.71) * mm, "end": v(-89.93, -10.2) * mm});
            skLineSegment(sketch, "E46.6.16.0", {"start": v(-78, -8.95) * mm, "end": v(-89.93, -10.2) * mm});
            skLineSegment(sketch, "E46.9.16.0", {"start": v(-78.15, -7.46) * mm, "end": v(-78, -8.95) * mm});
            skLineSegment(sketch, "E46.1.17.0", {"start": v(-76.94, -15.59) * mm, "end": v(-88.68, -18.08) * mm});
            skLineSegment(sketch, "E46.3.17.0", {"start": v(-88.68, -18.08) * mm, "end": v(-88.37, -19.55) * mm});
            skLineSegment(sketch, "E46.6.17.0", {"start": v(-76.63, -17.05) * mm, "end": v(-88.37, -19.55) * mm});
            skLineSegment(sketch, "E46.9.17.0", {"start": v(-76.94, -15.59) * mm, "end": v(-76.63, -17.05) * mm});
            skLineSegment(sketch, "E46.1.18.0", {"start": v(-74.89, -23.54) * mm, "end": v(-86.3, -27.25) * mm});
            skLineSegment(sketch, "E46.3.18.0", {"start": v(-86.3, -27.25) * mm, "end": v(-85.84, -28.68) * mm});
            skLineSegment(sketch, "E46.6.18.0", {"start": v(-74.43, -24.97) * mm, "end": v(-85.84, -28.68) * mm});
            skLineSegment(sketch, "E46.9.18.0", {"start": v(-74.89, -23.54) * mm, "end": v(-74.43, -24.97) * mm});
            skLineSegment(sketch, "E46.1.19.0", {"start": v(-72.02, -31.24) * mm, "end": v(-82.98, -36.12) * mm});
            skLineSegment(sketch, "E46.3.19.0", {"start": v(-82.98, -36.12) * mm, "end": v(-82.37, -37.5) * mm});
            skLineSegment(sketch, "E46.6.19.0", {"start": v(-71.4, -32.61) * mm, "end": v(-82.37, -37.5) * mm});
            skLineSegment(sketch, "E46.9.19.0", {"start": v(-72.02, -31.24) * mm, "end": v(-71.4, -32.61) * mm});
            skLineSegment(sketch, "E46.1.20.0", {"start": v(-68.36, -38.6) * mm, "end": v(-78.75, -44.6) * mm});
            skLineSegment(sketch, "E46.3.20.0", {"start": v(-78.75, -44.6) * mm, "end": v(-78, -45.9) * mm});
            skLineSegment(sketch, "E46.6.20.0", {"start": v(-67.6, -39.9) * mm, "end": v(-78, -45.9) * mm});
            skLineSegment(sketch, "E46.9.20.0", {"start": v(-68.36, -38.6) * mm, "end": v(-67.6, -39.9) * mm});
            skLineSegment(sketch, "E46.1.21.0", {"start": v(-63.95, -45.53) * mm, "end": v(-73.66, -52.59) * mm});
            skLineSegment(sketch, "E46.3.21.0", {"start": v(-73.66, -52.59) * mm, "end": v(-72.78, -53.8) * mm});
            skLineSegment(sketch, "E46.6.21.0", {"start": v(-63.07, -46.75) * mm, "end": v(-72.78, -53.8) * mm});
            skLineSegment(sketch, "E46.9.21.0", {"start": v(-63.95, -45.53) * mm, "end": v(-63.07, -46.75) * mm});
            skLineSegment(sketch, "E46.1.22.0", {"start": v(-58.84, -51.97) * mm, "end": v(-67.76, -60) * mm});
            skLineSegment(sketch, "E46.3.22.0", {"start": v(-67.76, -60) * mm, "end": v(-66.75, -61.11) * mm});
            skLineSegment(sketch, "E46.6.22.0", {"start": v(-57.84, -53.08) * mm, "end": v(-66.75, -61.11) * mm});
            skLineSegment(sketch, "E46.9.22.0", {"start": v(-58.84, -51.97) * mm, "end": v(-57.84, -53.08) * mm});
            skLineSegment(sketch, "E46.1.23.0", {"start": v(-53.08, -57.84) * mm, "end": v(-61.11, -66.75) * mm});
            skLineSegment(sketch, "E46.3.23.0", {"start": v(-61.11, -66.75) * mm, "end": v(-60, -67.76) * mm});
            skLineSegment(sketch, "E46.6.23.0", {"start": v(-51.97, -58.84) * mm, "end": v(-60, -67.76) * mm});
            skLineSegment(sketch, "E46.9.23.0", {"start": v(-53.08, -57.84) * mm, "end": v(-51.97, -58.84) * mm});
            skLineSegment(sketch, "E46.1.24.0", {"start": v(-46.75, -63.07) * mm, "end": v(-53.8, -72.78) * mm});
            skLineSegment(sketch, "E46.3.24.0", {"start": v(-53.8, -72.78) * mm, "end": v(-52.59, -73.66) * mm});
            skLineSegment(sketch, "E46.6.24.0", {"start": v(-45.53, -63.95) * mm, "end": v(-52.59, -73.66) * mm});
            skLineSegment(sketch, "E46.9.24.0", {"start": v(-46.75, -63.07) * mm, "end": v(-45.53, -63.95) * mm});
            skLineSegment(sketch, "E46.1.25.0", {"start": v(-39.9, -67.6) * mm, "end": v(-45.9, -78) * mm});
            skLineSegment(sketch, "E46.3.25.0", {"start": v(-45.9, -78) * mm, "end": v(-44.6, -78.75) * mm});
            skLineSegment(sketch, "E46.6.25.0", {"start": v(-38.6, -68.36) * mm, "end": v(-44.6, -78.75) * mm});
            skLineSegment(sketch, "E46.9.25.0", {"start": v(-39.9, -67.6) * mm, "end": v(-38.6, -68.36) * mm});
            skLineSegment(sketch, "E46.1.26.0", {"start": v(-32.61, -71.4) * mm, "end": v(-37.5, -82.37) * mm});
            skLineSegment(sketch, "E46.3.26.0", {"start": v(-37.5, -82.37) * mm, "end": v(-36.12, -82.98) * mm});
            skLineSegment(sketch, "E46.6.26.0", {"start": v(-31.24, -72.02) * mm, "end": v(-36.12, -82.98) * mm});
            skLineSegment(sketch, "E46.9.26.0", {"start": v(-32.61, -71.4) * mm, "end": v(-31.24, -72.02) * mm});
            skLineSegment(sketch, "E46.1.27.0", {"start": v(-24.97, -74.43) * mm, "end": v(-28.68, -85.84) * mm});
            skLineSegment(sketch, "E46.3.27.0", {"start": v(-28.68, -85.84) * mm, "end": v(-27.25, -86.3) * mm});
            skLineSegment(sketch, "E46.6.27.0", {"start": v(-23.54, -74.89) * mm, "end": v(-27.25, -86.3) * mm});
            skLineSegment(sketch, "E46.9.27.0", {"start": v(-24.97, -74.43) * mm, "end": v(-23.54, -74.89) * mm});
            skLineSegment(sketch, "E46.1.28.0", {"start": v(-17.05, -76.63) * mm, "end": v(-19.55, -88.37) * mm});
            skLineSegment(sketch, "E46.3.28.0", {"start": v(-19.55, -88.37) * mm, "end": v(-18.08, -88.68) * mm});
            skLineSegment(sketch, "E46.6.28.0", {"start": v(-15.59, -76.94) * mm, "end": v(-18.08, -88.68) * mm});
            skLineSegment(sketch, "E46.9.28.0", {"start": v(-17.05, -76.63) * mm, "end": v(-15.59, -76.94) * mm});
            skLineSegment(sketch, "E46.1.29.0", {"start": v(-8.95, -78) * mm, "end": v(-10.2, -89.93) * mm});
            skLineSegment(sketch, "E46.3.29.0", {"start": v(-10.2, -89.93) * mm, "end": v(-8.71, -90.08) * mm});
            skLineSegment(sketch, "E46.6.29.0", {"start": v(-7.46, -78.15) * mm, "end": v(-8.71, -90.08) * mm});
            skLineSegment(sketch, "E46.9.29.0", {"start": v(-8.95, -78) * mm, "end": v(-7.46, -78.15) * mm});
            skLineSegment(sketch, "E46.1.30.0", {"start": v(-0.75, -78.5) * mm, "end": v(-0.75, -90.5) * mm});
            skLineSegment(sketch, "E46.3.30.0", {"start": v(-0.75, -90.5) * mm, "end": v(0.75, -90.5) * mm});
            skLineSegment(sketch, "E46.6.30.0", {"start": v(0.75, -78.5) * mm, "end": v(0.75, -90.5) * mm});
            skLineSegment(sketch, "E46.9.30.0", {"start": v(-0.75, -78.5) * mm, "end": v(0.75, -78.5) * mm});
            skLineSegment(sketch, "E46.1.31.0", {"start": v(7.46, -78.15) * mm, "end": v(8.71, -90.08) * mm});
            skLineSegment(sketch, "E46.3.31.0", {"start": v(8.71, -90.08) * mm, "end": v(10.2, -89.93) * mm});
            skLineSegment(sketch, "E46.6.31.0", {"start": v(8.95, -78) * mm, "end": v(10.2, -89.93) * mm});
            skLineSegment(sketch, "E46.9.31.0", {"start": v(7.46, -78.15) * mm, "end": v(8.95, -78) * mm});
            skLineSegment(sketch, "E46.1.32.0", {"start": v(15.59, -76.94) * mm, "end": v(18.08, -88.68) * mm});
            skLineSegment(sketch, "E46.3.32.0", {"start": v(18.08, -88.68) * mm, "end": v(19.55, -88.37) * mm});
            skLineSegment(sketch, "E46.6.32.0", {"start": v(17.05, -76.63) * mm, "end": v(19.55, -88.37) * mm});
            skLineSegment(sketch, "E46.9.32.0", {"start": v(15.59, -76.94) * mm, "end": v(17.05, -76.63) * mm});
            skLineSegment(sketch, "E46.1.33.0", {"start": v(23.54, -74.89) * mm, "end": v(27.25, -86.3) * mm});
            skLineSegment(sketch, "E46.3.33.0", {"start": v(27.25, -86.3) * mm, "end": v(28.68, -85.84) * mm});
            skLineSegment(sketch, "E46.6.33.0", {"start": v(24.97, -74.43) * mm, "end": v(28.68, -85.84) * mm});
            skLineSegment(sketch, "E46.9.33.0", {"start": v(23.54, -74.89) * mm, "end": v(24.97, -74.43) * mm});
            skLineSegment(sketch, "E46.1.34.0", {"start": v(31.24, -72.02) * mm, "end": v(36.12, -82.98) * mm});
            skLineSegment(sketch, "E46.3.34.0", {"start": v(36.12, -82.98) * mm, "end": v(37.5, -82.37) * mm});
            skLineSegment(sketch, "E46.6.34.0", {"start": v(32.61, -71.4) * mm, "end": v(37.5, -82.37) * mm});
            skLineSegment(sketch, "E46.9.34.0", {"start": v(31.24, -72.02) * mm, "end": v(32.61, -71.4) * mm});
            skLineSegment(sketch, "E46.1.35.0", {"start": v(38.6, -68.36) * mm, "end": v(44.6, -78.75) * mm});
            skLineSegment(sketch, "E46.3.35.0", {"start": v(44.6, -78.75) * mm, "end": v(45.9, -78) * mm});
            skLineSegment(sketch, "E46.6.35.0", {"start": v(39.9, -67.6) * mm, "end": v(45.9, -78) * mm});
            skLineSegment(sketch, "E46.9.35.0", {"start": v(38.6, -68.36) * mm, "end": v(39.9, -67.6) * mm});
            skLineSegment(sketch, "E46.1.36.0", {"start": v(45.53, -63.95) * mm, "end": v(52.59, -73.66) * mm});
            skLineSegment(sketch, "E46.3.36.0", {"start": v(52.59, -73.66) * mm, "end": v(53.8, -72.78) * mm});
            skLineSegment(sketch, "E46.6.36.0", {"start": v(46.75, -63.07) * mm, "end": v(53.8, -72.78) * mm});
            skLineSegment(sketch, "E46.9.36.0", {"start": v(45.53, -63.95) * mm, "end": v(46.75, -63.07) * mm});
            skLineSegment(sketch, "E46.1.37.0", {"start": v(51.97, -58.84) * mm, "end": v(60, -67.76) * mm});
            skLineSegment(sketch, "E46.3.37.0", {"start": v(60, -67.76) * mm, "end": v(61.11, -66.75) * mm});
            skLineSegment(sketch, "E46.6.37.0", {"start": v(53.08, -57.84) * mm, "end": v(61.11, -66.75) * mm});
            skLineSegment(sketch, "E46.9.37.0", {"start": v(51.97, -58.84) * mm, "end": v(53.08, -57.84) * mm});
            skLineSegment(sketch, "E46.1.38.0", {"start": v(57.84, -53.08) * mm, "end": v(66.75, -61.11) * mm});
            skLineSegment(sketch, "E46.3.38.0", {"start": v(66.75, -61.11) * mm, "end": v(67.76, -60) * mm});
            skLineSegment(sketch, "E46.6.38.0", {"start": v(58.84, -51.97) * mm, "end": v(67.76, -60) * mm});
            skLineSegment(sketch, "E46.9.38.0", {"start": v(57.84, -53.08) * mm, "end": v(58.84, -51.97) * mm});
            skLineSegment(sketch, "E46.1.39.0", {"start": v(63.07, -46.75) * mm, "end": v(72.78, -53.8) * mm});
            skLineSegment(sketch, "E46.3.39.0", {"start": v(72.78, -53.8) * mm, "end": v(73.66, -52.59) * mm});
            skLineSegment(sketch, "E46.6.39.0", {"start": v(63.95, -45.53) * mm, "end": v(73.66, -52.59) * mm});
            skLineSegment(sketch, "E46.9.39.0", {"start": v(63.07, -46.75) * mm, "end": v(63.95, -45.53) * mm});
            skLineSegment(sketch, "E46.1.40.0", {"start": v(67.6, -39.9) * mm, "end": v(78, -45.9) * mm});
            skLineSegment(sketch, "E46.3.40.0", {"start": v(78, -45.9) * mm, "end": v(78.75, -44.6) * mm});
            skLineSegment(sketch, "E46.6.40.0", {"start": v(68.36, -38.6) * mm, "end": v(78.75, -44.6) * mm});
            skLineSegment(sketch, "E46.9.40.0", {"start": v(67.6, -39.9) * mm, "end": v(68.36, -38.6) * mm});
            skLineSegment(sketch, "E46.1.41.0", {"start": v(71.4, -32.61) * mm, "end": v(82.37, -37.5) * mm});
            skLineSegment(sketch, "E46.3.41.0", {"start": v(82.37, -37.5) * mm, "end": v(82.98, -36.12) * mm});
            skLineSegment(sketch, "E46.6.41.0", {"start": v(72.02, -31.24) * mm, "end": v(82.98, -36.12) * mm});
            skLineSegment(sketch, "E46.9.41.0", {"start": v(71.4, -32.61) * mm, "end": v(72.02, -31.24) * mm});
            skLineSegment(sketch, "E46.1.42.0", {"start": v(74.43, -24.97) * mm, "end": v(85.84, -28.68) * mm});
            skLineSegment(sketch, "E46.3.42.0", {"start": v(85.84, -28.68) * mm, "end": v(86.3, -27.25) * mm});
            skLineSegment(sketch, "E46.6.42.0", {"start": v(74.89, -23.54) * mm, "end": v(86.3, -27.25) * mm});
            skLineSegment(sketch, "E46.9.42.0", {"start": v(74.43, -24.97) * mm, "end": v(74.89, -23.54) * mm});
            skLineSegment(sketch, "E46.1.43.0", {"start": v(76.63, -17.05) * mm, "end": v(88.37, -19.55) * mm});
            skLineSegment(sketch, "E46.3.43.0", {"start": v(88.37, -19.55) * mm, "end": v(88.68, -18.08) * mm});
            skLineSegment(sketch, "E46.6.43.0", {"start": v(76.94, -15.59) * mm, "end": v(88.68, -18.08) * mm});
            skLineSegment(sketch, "E46.9.43.0", {"start": v(76.63, -17.05) * mm, "end": v(76.94, -15.59) * mm});
            skLineSegment(sketch, "E46.1.44.0", {"start": v(78, -8.95) * mm, "end": v(89.93, -10.2) * mm});
            skLineSegment(sketch, "E46.3.44.0", {"start": v(89.93, -10.2) * mm, "end": v(90.08, -8.71) * mm});
            skLineSegment(sketch, "E46.6.44.0", {"start": v(78.15, -7.46) * mm, "end": v(90.08, -8.71) * mm});
            skLineSegment(sketch, "E46.9.44.0", {"start": v(78, -8.95) * mm, "end": v(78.15, -7.46) * mm});
            skLineSegment(sketch, "E46.1.45.0", {"start": v(78.5, -0.75) * mm, "end": v(90.5, -0.75) * mm});
            skLineSegment(sketch, "E46.3.45.0", {"start": v(90.5, -0.75) * mm, "end": v(90.5, 0.75) * mm});
            skLineSegment(sketch, "E46.6.45.0", {"start": v(78.5, 0.75) * mm, "end": v(90.5, 0.75) * mm});
            skLineSegment(sketch, "E46.9.45.0", {"start": v(78.5, -0.75) * mm, "end": v(78.5, 0.75) * mm});
            skLineSegment(sketch, "E46.1.46.0", {"start": v(78.15, 7.46) * mm, "end": v(90.08, 8.71) * mm});
            skLineSegment(sketch, "E46.3.46.0", {"start": v(90.08, 8.71) * mm, "end": v(89.93, 10.2) * mm});
            skLineSegment(sketch, "E46.6.46.0", {"start": v(78, 8.95) * mm, "end": v(89.93, 10.2) * mm});
            skLineSegment(sketch, "E46.9.46.0", {"start": v(78.15, 7.46) * mm, "end": v(78, 8.95) * mm});
            skLineSegment(sketch, "E46.1.47.0", {"start": v(76.94, 15.59) * mm, "end": v(88.68, 18.08) * mm});
            skLineSegment(sketch, "E46.3.47.0", {"start": v(88.68, 18.08) * mm, "end": v(88.37, 19.55) * mm});
            skLineSegment(sketch, "E46.6.47.0", {"start": v(76.63, 17.05) * mm, "end": v(88.37, 19.55) * mm});
            skLineSegment(sketch, "E46.9.47.0", {"start": v(76.94, 15.59) * mm, "end": v(76.63, 17.05) * mm});
            skLineSegment(sketch, "E46.1.48.0", {"start": v(74.89, 23.54) * mm, "end": v(86.3, 27.25) * mm});
            skLineSegment(sketch, "E46.3.48.0", {"start": v(86.3, 27.25) * mm, "end": v(85.84, 28.68) * mm});
            skLineSegment(sketch, "E46.6.48.0", {"start": v(74.43, 24.97) * mm, "end": v(85.84, 28.68) * mm});
            skLineSegment(sketch, "E46.9.48.0", {"start": v(74.89, 23.54) * mm, "end": v(74.43, 24.97) * mm});
            skLineSegment(sketch, "E46.1.49.0", {"start": v(72.02, 31.24) * mm, "end": v(82.98, 36.12) * mm});
            skLineSegment(sketch, "E46.3.49.0", {"start": v(82.98, 36.12) * mm, "end": v(82.37, 37.5) * mm});
            skLineSegment(sketch, "E46.6.49.0", {"start": v(71.4, 32.61) * mm, "end": v(82.37, 37.5) * mm});
            skLineSegment(sketch, "E46.9.49.0", {"start": v(72.02, 31.24) * mm, "end": v(71.4, 32.61) * mm});
            skLineSegment(sketch, "E46.1.50.0", {"start": v(68.36, 38.6) * mm, "end": v(78.75, 44.6) * mm});
            skLineSegment(sketch, "E46.3.50.0", {"start": v(78.75, 44.6) * mm, "end": v(78, 45.9) * mm});
            skLineSegment(sketch, "E46.6.50.0", {"start": v(67.6, 39.9) * mm, "end": v(78, 45.9) * mm});
            skLineSegment(sketch, "E46.9.50.0", {"start": v(68.36, 38.6) * mm, "end": v(67.6, 39.9) * mm});
            skLineSegment(sketch, "E46.1.51.0", {"start": v(63.95, 45.53) * mm, "end": v(73.66, 52.59) * mm});
            skLineSegment(sketch, "E46.3.51.0", {"start": v(73.66, 52.59) * mm, "end": v(72.78, 53.8) * mm});
            skLineSegment(sketch, "E46.6.51.0", {"start": v(63.07, 46.75) * mm, "end": v(72.78, 53.8) * mm});
            skLineSegment(sketch, "E46.9.51.0", {"start": v(63.95, 45.53) * mm, "end": v(63.07, 46.75) * mm});
            skLineSegment(sketch, "E46.1.52.0", {"start": v(58.84, 51.97) * mm, "end": v(67.76, 60) * mm});
            skLineSegment(sketch, "E46.3.52.0", {"start": v(67.76, 60) * mm, "end": v(66.75, 61.11) * mm});
            skLineSegment(sketch, "E46.6.52.0", {"start": v(57.84, 53.08) * mm, "end": v(66.75, 61.11) * mm});
            skLineSegment(sketch, "E46.9.52.0", {"start": v(58.84, 51.97) * mm, "end": v(57.84, 53.08) * mm});
            skLineSegment(sketch, "E46.1.53.0", {"start": v(53.08, 57.84) * mm, "end": v(61.11, 66.75) * mm});
            skLineSegment(sketch, "E46.3.53.0", {"start": v(61.11, 66.75) * mm, "end": v(60, 67.76) * mm});
            skLineSegment(sketch, "E46.6.53.0", {"start": v(51.97, 58.84) * mm, "end": v(60, 67.76) * mm});
            skLineSegment(sketch, "E46.9.53.0", {"start": v(53.08, 57.84) * mm, "end": v(51.97, 58.84) * mm});
            skLineSegment(sketch, "E46.1.54.0", {"start": v(46.75, 63.07) * mm, "end": v(53.8, 72.78) * mm});
            skLineSegment(sketch, "E46.3.54.0", {"start": v(53.8, 72.78) * mm, "end": v(52.59, 73.66) * mm});
            skLineSegment(sketch, "E46.6.54.0", {"start": v(45.53, 63.95) * mm, "end": v(52.59, 73.66) * mm});
            skLineSegment(sketch, "E46.9.54.0", {"start": v(46.75, 63.07) * mm, "end": v(45.53, 63.95) * mm});
            skLineSegment(sketch, "E46.1.55.0", {"start": v(39.9, 67.6) * mm, "end": v(45.9, 78) * mm});
            skLineSegment(sketch, "E46.3.55.0", {"start": v(45.9, 78) * mm, "end": v(44.6, 78.75) * mm});
            skLineSegment(sketch, "E46.6.55.0", {"start": v(38.6, 68.36) * mm, "end": v(44.6, 78.75) * mm});
            skLineSegment(sketch, "E46.9.55.0", {"start": v(39.9, 67.6) * mm, "end": v(38.6, 68.36) * mm});
            skLineSegment(sketch, "E46.1.56.0", {"start": v(32.61, 71.4) * mm, "end": v(37.5, 82.37) * mm});
            skLineSegment(sketch, "E46.3.56.0", {"start": v(37.5, 82.37) * mm, "end": v(36.12, 82.98) * mm});
            skLineSegment(sketch, "E46.6.56.0", {"start": v(31.24, 72.02) * mm, "end": v(36.12, 82.98) * mm});
            skLineSegment(sketch, "E46.9.56.0", {"start": v(32.61, 71.4) * mm, "end": v(31.24, 72.02) * mm});
            skLineSegment(sketch, "E46.1.57.0", {"start": v(24.97, 74.43) * mm, "end": v(28.68, 85.84) * mm});
            skLineSegment(sketch, "E46.3.57.0", {"start": v(28.68, 85.84) * mm, "end": v(27.25, 86.3) * mm});
            skLineSegment(sketch, "E46.6.57.0", {"start": v(23.54, 74.89) * mm, "end": v(27.25, 86.3) * mm});
            skLineSegment(sketch, "E46.9.57.0", {"start": v(24.97, 74.43) * mm, "end": v(23.54, 74.89) * mm});
            skLineSegment(sketch, "E46.1.58.0", {"start": v(17.05, 76.63) * mm, "end": v(19.55, 88.37) * mm});
            skLineSegment(sketch, "E46.3.58.0", {"start": v(19.55, 88.37) * mm, "end": v(18.08, 88.68) * mm});
            skLineSegment(sketch, "E46.6.58.0", {"start": v(15.59, 76.94) * mm, "end": v(18.08, 88.68) * mm});
            skLineSegment(sketch, "E46.9.58.0", {"start": v(17.05, 76.63) * mm, "end": v(15.59, 76.94) * mm});
            skLineSegment(sketch, "E46.1.59.0", {"start": v(8.95, 78) * mm, "end": v(10.2, 89.93) * mm});
            skLineSegment(sketch, "E46.3.59.0", {"start": v(10.2, 89.93) * mm, "end": v(8.71, 90.08) * mm});
            skLineSegment(sketch, "E46.6.59.0", {"start": v(7.46, 78.15) * mm, "end": v(8.71, 90.08) * mm});
            skLineSegment(sketch, "E46.9.59.0", {"start": v(8.95, 78) * mm, "end": v(7.46, 78.15) * mm});
            skSolve(sketch);
        }
        {
            var Q0;
            Q0 = qSketchRegion(id + "F27", true);
            extrude(context, id + "F28", {"entities" : qUnion([Q0]), "operationType" : NewBodyOperationType.REMOVE, "oppositeDirection" : true, "depth" : 0.2 * mm, "offsetDistance" : 25 * mm});
        }
        {
            var Q0;
            Q0=makeQuery(id+"F26.boolean.opBoolean","COPY",FACE,{"derivedFrom":makeQuery(id+"F26.opExtrude","CAP_FACE",FACE,{"disambiguationData":[OSD([sQuery(id+"F25.wireOp",EDGE,"E41.bottom"),sQuery(id+"F25.wireOp",EDGE,"E41.top"),sQuery(id+"F25.wireOp",EDGE,"E41.left"),sQuery(id+"F25.wireOp",EDGE,"E41.right")])],"isStart":false})});
            extrude(context, id + "F29", {"entities" : qUnion([Q0]), "depth" : 1 * mm, "offsetDistance" : 25 * mm});
        }
        {
            var Q0;
            Q0=makeQuery(id+"F28.boolean.opBoolean","COPY",FACE,{"derivedFrom":makeQuery(id+"F28.opExtrude","CAP_FACE",FACE,{"disambiguationData":[OSD([sQuery(id+"F27.wireOp",EDGE,"E46.1.59.0"),sQuery(id+"F27.wireOp",EDGE,"E46.3.59.0"),sQuery(id+"F27.wireOp",EDGE,"E46.6.59.0"),sQuery(id+"F27.wireOp",EDGE,"E46.9.59.0")])],"isStart":false})});
            extrude(context, id + "F30", {"entities" : qUnion([Q0]), "depth" : 0.4 * mm, "offsetDistance" : 25 * mm});
        }
        {
            var Q0;
            Q0=makeQuery(id+"F15.opExtrude","CAP_FACE",FACE,{"disambiguationData":[OSD([sQuery(id+"F14.wireOp",EDGE,"E21.0"),sQuery(id+"F14.wireOp",EDGE,"E22"),sQuery(id+"F14.wireOp",EDGE,"E23"),sQuery(id+"F14.wireOp",EDGE,"E24"),sQuery(id+"F14.wireOp",EDGE,"E25.MirrorCS"),sQuery(id+"F14.wireOp",EDGE,"E26.MirrorCS"),sQuery(id+"F14.wireOp",EDGE,"E27.1.0"),sQuery(id+"F14.wireOp",EDGE,"E27.1.1"),sQuery(id+"F14.wireOp",EDGE,"E27.1.2"),sQuery(id+"F14.wireOp",EDGE,"E27.1.3"),sQuery(id+"F14.wireOp",EDGE,"E27.2.0"),sQuery(id+"F14.wireOp",EDGE,"E27.2.1"),sQuery(id+"F14.wireOp",EDGE,"E27.2.2"),sQuery(id+"F14.wireOp",EDGE,"E27.2.3"),sQuery(id+"F14.wireOp",EDGE,"E28.1.3.0"),sQuery(id+"F14.wireOp",EDGE,"E28.3.3.0"),sQuery(id+"F14.wireOp",EDGE,"E28.6.3.0"),sQuery(id+"F14.wireOp",EDGE,"E28.9.3.0"),sQuery(id+"F14.wireOp",EDGE,"E28.1.4.0"),sQuery(id+"F14.wireOp",EDGE,"E28.3.4.0"),sQuery(id+"F14.wireOp",EDGE,"E28.6.4.0"),sQuery(id+"F14.wireOp",EDGE,"E28.9.4.0"),sQuery(id+"F14.wireOp",EDGE,"E28.1.5.0"),sQuery(id+"F14.wireOp",EDGE,"E28.3.5.0"),sQuery(id+"F14.wireOp",EDGE,"E28.6.5.0"),sQuery(id+"F14.wireOp",EDGE,"E28.9.5.0"),sQuery(id+"F14.wireOp",EDGE,"E28.1.6.0"),sQuery(id+"F14.wireOp",EDGE,"E28.3.6.0"),sQuery(id+"F14.wireOp",EDGE,"E28.6.6.0"),sQuery(id+"F14.wireOp",EDGE,"E28.9.6.0"),sQuery(id+"F14.wireOp",EDGE,"E28.1.7.0"),sQuery(id+"F14.wireOp",EDGE,"E28.3.7.0"),sQuery(id+"F14.wireOp",EDGE,"E28.6.7.0"),sQuery(id+"F14.wireOp",EDGE,"E28.9.7.0"),sQuery(id+"F14.wireOp",EDGE,"E28.1.8.0"),sQuery(id+"F14.wireOp",EDGE,"E28.3.8.0"),sQuery(id+"F14.wireOp",EDGE,"E28.6.8.0"),sQuery(id+"F14.wireOp",EDGE,"E28.9.8.0"),sQuery(id+"F14.wireOp",EDGE,"E28.1.9.0"),sQuery(id+"F14.wireOp",EDGE,"E28.3.9.0"),sQuery(id+"F14.wireOp",EDGE,"E28.6.9.0"),sQuery(id+"F14.wireOp",EDGE,"E28.9.9.0"),sQuery(id+"F14.wireOp",EDGE,"E28.1.10.0"),sQuery(id+"F14.wireOp",EDGE,"E28.3.10.0"),sQuery(id+"F14.wireOp",EDGE,"E28.6.10.0"),sQuery(id+"F14.wireOp",EDGE,"E28.9.10.0"),sQuery(id+"F14.wireOp",EDGE,"E28.1.11.0"),sQuery(id+"F14.wireOp",EDGE,"E28.3.11.0"),sQuery(id+"F14.wireOp",EDGE,"E28.6.11.0"),sQuery(id+"F14.wireOp",EDGE,"E28.9.11.0"),sQuery(id+"F14.wireOp",EDGE,"E28.1.12.0"),sQuery(id+"F14.wireOp",EDGE,"E28.3.12.0"),sQuery(id+"F14.wireOp",EDGE,"E28.6.12.0"),sQuery(id+"F14.wireOp",EDGE,"E28.9.12.0"),sQuery(id+"F14.wireOp",EDGE,"E28.1.13.0"),sQuery(id+"F14.wireOp",EDGE,"E28.3.13.0"),sQuery(id+"F14.wireOp",EDGE,"E28.6.13.0"),sQuery(id+"F14.wireOp",EDGE,"E28.9.13.0"),sQuery(id+"F14.wireOp",EDGE,"E28.1.14.0"),sQuery(id+"F14.wireOp",EDGE,"E28.3.14.0"),sQuery(id+"F14.wireOp",EDGE,"E28.6.14.0"),sQuery(id+"F14.wireOp",EDGE,"E28.9.14.0"),sQuery(id+"F14.wireOp",EDGE,"E28.1.15.0"),sQuery(id+"F14.wireOp",EDGE,"E28.3.15.0"),sQuery(id+"F14.wireOp",EDGE,"E28.6.15.0"),sQuery(id+"F14.wireOp",EDGE,"E28.9.15.0"),sQuery(id+"F14.wireOp",EDGE,"E28.1.16.0"),sQuery(id+"F14.wireOp",EDGE,"E28.3.16.0"),sQuery(id+"F14.wireOp",EDGE,"E28.6.16.0"),sQuery(id+"F14.wireOp",EDGE,"E28.9.16.0"),sQuery(id+"F14.wireOp",EDGE,"E28.1.17.0"),sQuery(id+"F14.wireOp",EDGE,"E28.3.17.0"),sQuery(id+"F14.wireOp",EDGE,"E28.6.17.0"),sQuery(id+"F14.wireOp",EDGE,"E28.9.17.0"),sQuery(id+"F14.wireOp",EDGE,"E28.1.18.0"),sQuery(id+"F14.wireOp",EDGE,"E28.3.18.0"),sQuery(id+"F14.wireOp",EDGE,"E28.6.18.0"),sQuery(id+"F14.wireOp",EDGE,"E28.9.18.0"),sQuery(id+"F14.wireOp",EDGE,"E28.1.19.0"),sQuery(id+"F14.wireOp",EDGE,"E28.3.19.0"),sQuery(id+"F14.wireOp",EDGE,"E28.6.19.0"),sQuery(id+"F14.wireOp",EDGE,"E28.9.19.0"),sQuery(id+"F14.wireOp",EDGE,"E28.1.20.0"),sQuery(id+"F14.wireOp",EDGE,"E28.3.20.0"),sQuery(id+"F14.wireOp",EDGE,"E28.6.20.0"),sQuery(id+"F14.wireOp",EDGE,"E28.9.20.0"),sQuery(id+"F14.wireOp",EDGE,"E28.1.21.0"),sQuery(id+"F14.wireOp",EDGE,"E28.3.21.0"),sQuery(id+"F14.wireOp",EDGE,"E28.6.21.0"),sQuery(id+"F14.wireOp",EDGE,"E28.9.21.0"),sQuery(id+"F14.wireOp",EDGE,"E28.1.22.0"),sQuery(id+"F14.wireOp",EDGE,"E28.3.22.0"),sQuery(id+"F14.wireOp",EDGE,"E28.6.22.0"),sQuery(id+"F14.wireOp",EDGE,"E28.9.22.0"),sQuery(id+"F14.wireOp",EDGE,"E28.1.23.0"),sQuery(id+"F14.wireOp",EDGE,"E28.3.23.0"),sQuery(id+"F14.wireOp",EDGE,"E28.6.23.0"),sQuery(id+"F14.wireOp",EDGE,"E28.9.23.0"),sQuery(id+"F14.wireOp",EDGE,"E28.1.24.0"),sQuery(id+"F14.wireOp",EDGE,"E28.3.24.0"),sQuery(id+"F14.wireOp",EDGE,"E28.6.24.0"),sQuery(id+"F14.wireOp",EDGE,"E28.9.24.0"),sQuery(id+"F14.wireOp",EDGE,"E28.1.25.0"),sQuery(id+"F14.wireOp",EDGE,"E28.3.25.0"),sQuery(id+"F14.wireOp",EDGE,"E28.6.25.0"),sQuery(id+"F14.wireOp",EDGE,"E28.9.25.0"),sQuery(id+"F14.wireOp",EDGE,"E28.1.26.0"),sQuery(id+"F14.wireOp",EDGE,"E28.3.26.0"),sQuery(id+"F14.wireOp",EDGE,"E28.6.26.0"),sQuery(id+"F14.wireOp",EDGE,"E28.9.26.0"),sQuery(id+"F14.wireOp",EDGE,"E28.1.27.0"),sQuery(id+"F14.wireOp",EDGE,"E28.3.27.0"),sQuery(id+"F14.wireOp",EDGE,"E28.6.27.0"),sQuery(id+"F14.wireOp",EDGE,"E28.9.27.0"),sQuery(id+"F14.wireOp",EDGE,"E28.1.28.0"),sQuery(id+"F14.wireOp",EDGE,"E28.3.28.0"),sQuery(id+"F14.wireOp",EDGE,"E28.6.28.0"),sQuery(id+"F14.wireOp",EDGE,"E28.9.28.0"),sQuery(id+"F14.wireOp",EDGE,"E28.1.29.0"),sQuery(id+"F14.wireOp",EDGE,"E28.3.29.0"),sQuery(id+"F14.wireOp",EDGE,"E28.6.29.0"),sQuery(id+"F14.wireOp",EDGE,"E28.9.29.0"),sQuery(id+"F14.wireOp",EDGE,"E28.1.30.0"),sQuery(id+"F14.wireOp",EDGE,"E28.3.30.0"),sQuery(id+"F14.wireOp",EDGE,"E28.6.30.0"),sQuery(id+"F14.wireOp",EDGE,"E28.9.30.0"),sQuery(id+"F14.wireOp",EDGE,"E28.1.31.0"),sQuery(id+"F14.wireOp",EDGE,"E28.3.31.0"),sQuery(id+"F14.wireOp",EDGE,"E28.6.31.0"),sQuery(id+"F14.wireOp",EDGE,"E28.9.31.0"),sQuery(id+"F14.wireOp",EDGE,"E28.1.32.0"),sQuery(id+"F14.wireOp",EDGE,"E28.3.32.0"),sQuery(id+"F14.wireOp",EDGE,"E28.6.32.0"),sQuery(id+"F14.wireOp",EDGE,"E28.9.32.0"),sQuery(id+"F14.wireOp",EDGE,"E28.1.33.0"),sQuery(id+"F14.wireOp",EDGE,"E28.3.33.0"),sQuery(id+"F14.wireOp",EDGE,"E28.6.33.0"),sQuery(id+"F14.wireOp",EDGE,"E28.9.33.0"),sQuery(id+"F14.wireOp",EDGE,"E28.1.34.0"),sQuery(id+"F14.wireOp",EDGE,"E28.3.34.0"),sQuery(id+"F14.wireOp",EDGE,"E28.6.34.0"),sQuery(id+"F14.wireOp",EDGE,"E28.9.34.0"),sQuery(id+"F14.wireOp",EDGE,"E28.1.35.0"),sQuery(id+"F14.wireOp",EDGE,"E28.3.35.0"),sQuery(id+"F14.wireOp",EDGE,"E28.6.35.0"),sQuery(id+"F14.wireOp",EDGE,"E28.9.35.0"),sQuery(id+"F14.wireOp",EDGE,"E28.1.36.0"),sQuery(id+"F14.wireOp",EDGE,"E28.3.36.0"),sQuery(id+"F14.wireOp",EDGE,"E28.6.36.0"),sQuery(id+"F14.wireOp",EDGE,"E28.9.36.0"),sQuery(id+"F14.wireOp",EDGE,"E28.1.37.0"),sQuery(id+"F14.wireOp",EDGE,"E28.3.37.0"),sQuery(id+"F14.wireOp",EDGE,"E28.6.37.0"),sQuery(id+"F14.wireOp",EDGE,"E28.9.37.0"),sQuery(id+"F14.wireOp",EDGE,"E28.1.38.0"),sQuery(id+"F14.wireOp",EDGE,"E28.3.38.0"),sQuery(id+"F14.wireOp",EDGE,"E28.6.38.0"),sQuery(id+"F14.wireOp",EDGE,"E28.9.38.0"),sQuery(id+"F14.wireOp",EDGE,"E28.1.39.0"),sQuery(id+"F14.wireOp",EDGE,"E28.3.39.0"),sQuery(id+"F14.wireOp",EDGE,"E28.6.39.0"),sQuery(id+"F14.wireOp",EDGE,"E28.9.39.0")])],"isStart":false});
            var sketch = newSketch(context, id + "F31", { "sketchPlane" : qUnion([Q0])});
            skCircle(sketch, "E47.0", {"center": v(0, 0) * mm, "radius": 5 * mm});
            skCircle(sketch, "E48.0", {"center": v(0, 0) * mm, "radius": 3 * mm});
            skSolve(sketch);
        }
        {
            var Q0;
            Q0 = qSketchRegion(id + "F31", true);
            extrude(context, id + "F32", {"entities" : qUnion([Q0]), "operationType" : NewBodyOperationType.ADD, "depth" : 5 * mm, "offsetDistance" : 25 * mm});
        }
        {
            var Q0;
            Q0=makeQuery(id+"F32.opExtrude","CAP_FACE",FACE,{"disambiguationData":[OSD([sQuery(id+"F31.wireOp",EDGE,"E47.0"),sQuery(id+"F31.wireOp",EDGE,"E48.0")])],"isStart":false});
            var sketch = newSketch(context, id + "F33", { "sketchPlane" : qUnion([Q0])});
            skCircle(sketch, "E49.0", {"center": v(0, 0) * mm, "radius": 5 * mm});
            skCircle(sketch, "E50.0", {"center": v(0, 0) * mm, "radius": 3 * mm});
            skLineSegment(sketch, "E51", {"start": v(3, 4) * mm, "end": v(1.5, 50) * mm});
            skLineSegment(sketch, "E52", {"start": v(1.5, 50) * mm, "end": v(0, 50) * mm});
            skLineSegment(sketch, "E53.MirrorCS", {"start": v(-1.5, 50) * mm, "end": v(0, 50) * mm});
            skLineSegment(sketch, "E54.MirrorCS", {"start": v(-3, 4) * mm, "end": v(-1.5, 50) * mm});
            skSolve(sketch);
        }
        {
            var Q0;
            Q0 = qSketchRegion(id + "F33", true);
            extrude(context, id + "F34", {"entities" : qUnion([Q0]), "operationType" : NewBodyOperationType.ADD, "depth" : 1 * mm, "offsetDistance" : 25 * mm});
        }
        {
            var Q0;
            Q0=makeQuery(id+"F6.opExtrude","CAP_FACE",FACE,{"disambiguationData":[OSD([sQuery(id+"F0.wireOp",EDGE,"E0")])],"isStart":false});
            var sketch = newSketch(context, id + "F35", { "sketchPlane" : qUnion([Q0])});
            skCircle(sketch, "E55", {"center": v(0, 0) * mm, "radius": 5 * mm});
            skLineSegment(sketch, "E56", {"start": v(2, 4.58) * mm, "end": v(0.5, 80) * mm});
            skLineSegment(sketch, "E57", {"start": v(0.5, 80) * mm, "end": v(0, 80) * mm});
            skLineSegment(sketch, "E58.MirrorCS", {"start": v(-0.5, 80) * mm, "end": v(0, 80) * mm});
            skLineSegment(sketch, "E59.MirrorCS", {"start": v(-2, 4.58) * mm, "end": v(-0.5, 80) * mm});
            skSolve(sketch);
        }
        {
            var Q0;
            Q0 = qSketchRegion(id + "F35", true);
            extrude(context, id + "F36", {"entities" : qUnion([Q0]), "operationType" : NewBodyOperationType.ADD, "oppositeDirection" : true, "depth" : 1 * mm, "offsetDistance" : 25 * mm});
        }
    });
